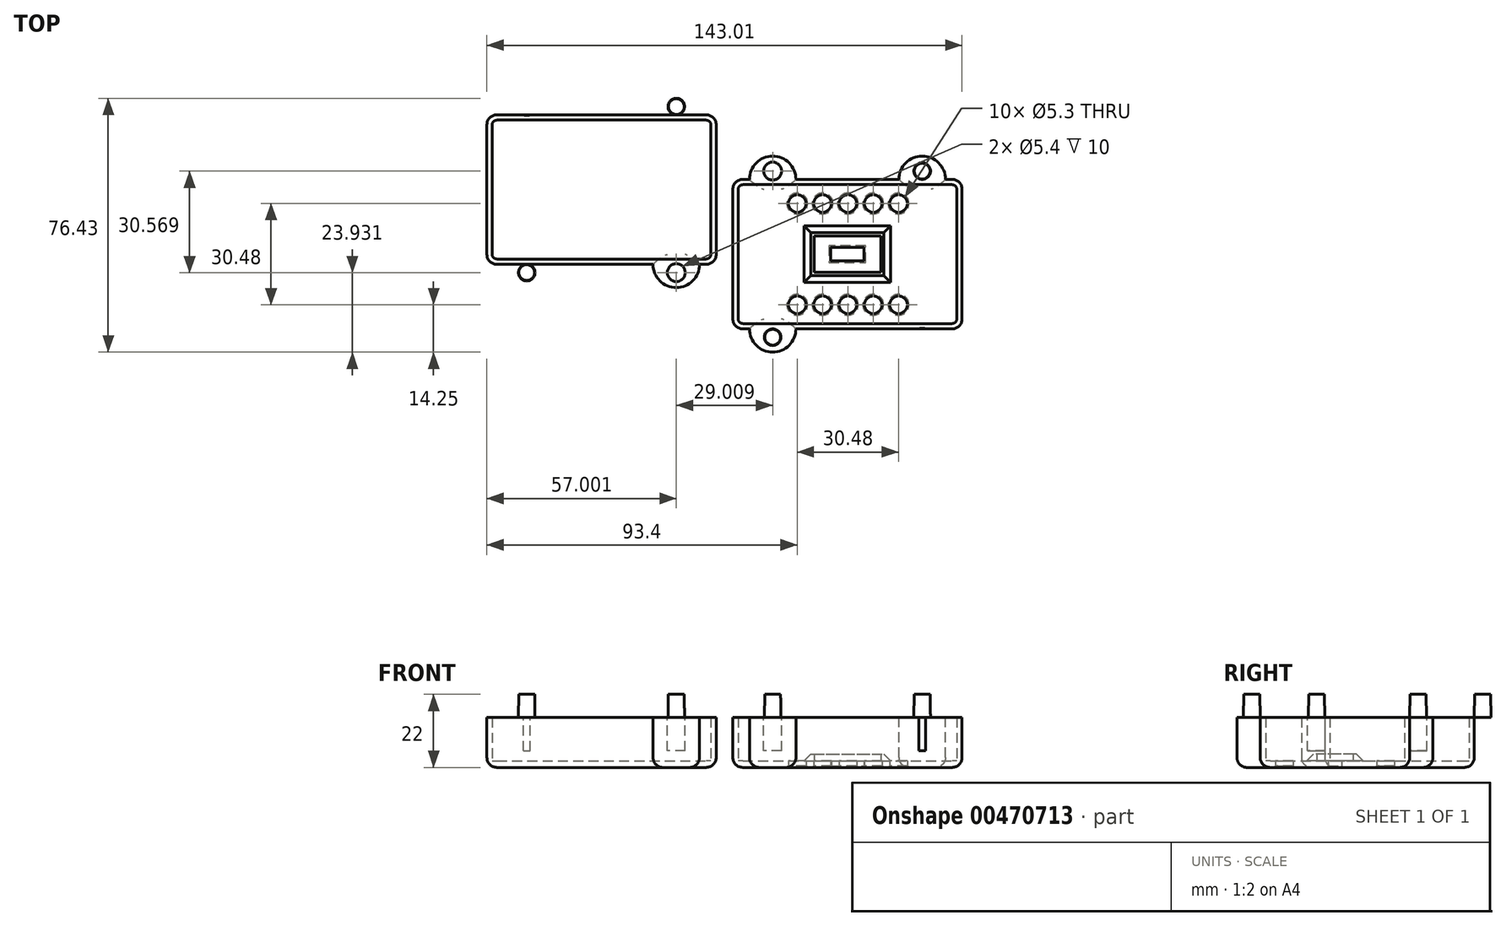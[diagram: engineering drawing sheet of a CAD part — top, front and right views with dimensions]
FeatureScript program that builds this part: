
annotation { "Feature Type Name" : "Feature", "Feature Type Description" : "" }
export const myFeature = defineFeature(function(context is Context, id is Id, definition is map)
    precondition{}
    {
        {
            var Q0;
            Q0=qCreatedBy(makeId("Top.planeOp"),FACE);
            var sketch = newSketch(context, id + "F0", { "sketchPlane" : qUnion([Q0])});
            skLineSegment(sketch, "E0.bottom", {"start": v(3, 0) * mm, "end": v(66, 0) * mm});
            skLineSegment(sketch, "E0.top", {"start": v(3, 45) * mm, "end": v(66, 45) * mm});
            skLineSegment(sketch, "E0.left", {"start": v(0, 3) * mm, "end": v(0, 42) * mm});
            skLineSegment(sketch, "E0.right", {"start": v(69, 3) * mm, "end": v(69, 42) * mm});
            skPoint(sketch, "E1.visualSharp", {"position": v(0, 45) * mm});
            skArc(sketch, "E1.filletArc", {"start": v(3, 45) * mm, "mid": v(0.88, 44.12) * mm, "end": v(0, 42) * mm});
            skPoint(sketch, "E2.visualSharp", {"position": v(69, 45) * mm});
            skArc(sketch, "E2.filletArc", {"start": v(69, 42) * mm, "mid": v(68.12, 44.12) * mm, "end": v(66, 45) * mm});
            skPoint(sketch, "E3.visualSharp", {"position": v(0, 0) * mm});
            skArc(sketch, "E3.filletArc", {"start": v(0, 3) * mm, "mid": v(0.88, 0.88) * mm, "end": v(3, 0) * mm});
            skPoint(sketch, "E4.visualSharp", {"position": v(69, 0) * mm});
            skArc(sketch, "E4.filletArc", {"start": v(66, 0) * mm, "mid": v(68.12, 0.88) * mm, "end": v(69, 3) * mm});
            skLineSegment(sketch, "E5.0", {"start": v(3, 43.4) * mm, "end": v(67.13, 43.4) * mm});
            skLineSegment(sketch, "E6.0", {"start": v(1.6, 3) * mm, "end": v(1.6, 42) * mm});
            skLineSegment(sketch, "E7.0", {"start": v(67.4, 3) * mm, "end": v(67.4, 42) * mm});
            skLineSegment(sketch, "E8.0", {"start": v(3, 1.6) * mm, "end": v(67.13, 1.6) * mm});
            skPoint(sketch, "E9", {"position": v(34.5, 22.5) * mm});
            skPoint(sketch, "E9.positionSnap0", {"position": v(0, 22.5) * mm});
            skPoint(sketch, "E9.positionSnap1", {"position": v(34.5, 45) * mm});
            skLineSegment(sketch, "E10.bottom", {"start": v(4.5, 42.5) * mm, "end": v(64.5, 42.5) * mm});
            skLineSegment(sketch, "E10.top", {"start": v(4.5, 2.5) * mm, "end": v(64.5, 2.5) * mm});
            skLineSegment(sketch, "E10.left", {"start": v(4.5, 42.5) * mm, "end": v(4.5, 2.5) * mm});
            skLineSegment(sketch, "E10.right", {"start": v(64.5, 42.5) * mm, "end": v(64.5, 2.5) * mm});
            skLineSegment(sketch, "E11", {"start": v(34.5, 42.5) * mm, "end": v(34.5, 2.5) * mm, "construction": true});
            skLineSegment(sketch, "E12", {"start": v(4.5, 22.5) * mm, "end": v(64.5, 22.5) * mm, "construction": true});
            skCircle(sketch, "E13", {"center": v(6.5, 40.5) * mm, "radius": 1 * mm});
            skCircle(sketch, "E14", {"center": v(62.5, 40.5) * mm, "radius": 1 * mm});
            skCircle(sketch, "E15", {"center": v(62.5, 4.5) * mm, "radius": 1 * mm});
            skCircle(sketch, "E16", {"center": v(6.5, 4.5) * mm, "radius": 1 * mm});
            skLineSegment(sketch, "E17.0", {"start": v(2.5, 39) * mm, "end": v(62.5, 39) * mm, "construction": true});
            skLineSegment(sketch, "E18.0", {"start": v(2.5, 6) * mm, "end": v(62.5, 6) * mm, "construction": true});
            skLineSegment(sketch, "E19.0", {"start": v(58.5, 42.5) * mm, "end": v(58.5, 2.5) * mm, "construction": true});
            skLineSegment(sketch, "E20.0", {"start": v(10.5, 42.5) * mm, "end": v(10.5, 2.5) * mm, "construction": true});
            skCircle(sketch, "E21", {"center": v(10.5, 39) * mm, "radius": 0.5 * mm, "construction": true});
            skCircle(sketch, "E22.1.0.0", {"center": v(13.04, 39) * mm, "radius": 0.5 * mm, "construction": true});
            skCircle(sketch, "E22.2.0.0", {"center": v(15.58, 39) * mm, "radius": 0.5 * mm, "construction": true});
            skCircle(sketch, "E22.3.0.0", {"center": v(18.12, 39) * mm, "radius": 0.5 * mm, "construction": true});
            skCircle(sketch, "E22.4.0.0", {"center": v(20.66, 39) * mm, "radius": 0.5 * mm, "construction": true});
            skCircle(sketch, "E22.5.0.0", {"center": v(23.2, 39) * mm, "radius": 0.5 * mm, "construction": true});
            skCircle(sketch, "E22.6.0.0", {"center": v(25.74, 39) * mm, "radius": 0.5 * mm, "construction": true});
            skCircle(sketch, "E22.7.0.0", {"center": v(28.28, 39) * mm, "radius": 0.5 * mm, "construction": true});
            skCircle(sketch, "E22.8.0.0", {"center": v(30.82, 39) * mm, "radius": 0.5 * mm, "construction": true});
            skCircle(sketch, "E22.9.0.0", {"center": v(33.36, 39) * mm, "radius": 0.5 * mm, "construction": true});
            skCircle(sketch, "E22.10.0.0", {"center": v(35.9, 39) * mm, "radius": 0.5 * mm, "construction": true});
            skCircle(sketch, "E22.11.0.0", {"center": v(38.44, 39) * mm, "radius": 0.5 * mm, "construction": true});
            skCircle(sketch, "E22.12.0.0", {"center": v(40.98, 39) * mm, "radius": 0.5 * mm, "construction": true});
            skCircle(sketch, "E22.13.0.0", {"center": v(43.52, 39) * mm, "radius": 0.5 * mm, "construction": true});
            skCircle(sketch, "E22.14.0.0", {"center": v(46.06, 39) * mm, "radius": 0.5 * mm, "construction": true});
            skCircle(sketch, "E22.15.0.0", {"center": v(48.6, 39) * mm, "radius": 0.5 * mm, "construction": true});
            skCircle(sketch, "E22.16.0.0", {"center": v(51.14, 39) * mm, "radius": 0.5 * mm, "construction": true});
            skCircle(sketch, "E22.17.0.0", {"center": v(53.68, 39) * mm, "radius": 0.5 * mm, "construction": true});
            skCircle(sketch, "E22.18.0.0", {"center": v(56.22, 39) * mm, "radius": 0.5 * mm, "construction": true});
            skCircle(sketch, "E22.19.0.0", {"center": v(58.76, 39) * mm, "radius": 0.5 * mm, "construction": true});
            skLineSegment(sketch, "E22.direction1", {"start": v(10.5, 39) * mm, "end": v(13.04, 39) * mm, "construction": true});
            skCircle(sketch, "E23.1.0.0", {"center": v(10.5, 36.46) * mm, "radius": 0.5 * mm, "construction": true});
            skCircle(sketch, "E23.1.0.1", {"center": v(11.04, 36.46) * mm, "radius": 0.5 * mm, "construction": true});
            skCircle(sketch, "E23.1.0.2", {"center": v(13.58, 36.46) * mm, "radius": 0.5 * mm, "construction": true});
            skCircle(sketch, "E23.1.0.3", {"center": v(18.12, 36.46) * mm, "radius": 0.5 * mm, "construction": true});
            skCircle(sketch, "E23.1.0.4", {"center": v(18.66, 36.46) * mm, "radius": 0.5 * mm, "construction": true});
            skCircle(sketch, "E23.1.0.5", {"center": v(21.2, 36.46) * mm, "radius": 0.5 * mm, "construction": true});
            skCircle(sketch, "E23.1.0.6", {"center": v(25.74, 36.46) * mm, "radius": 0.5 * mm, "construction": true});
            skCircle(sketch, "E23.1.0.7", {"center": v(26.28, 36.46) * mm, "radius": 0.5 * mm, "construction": true});
            skCircle(sketch, "E23.1.0.8", {"center": v(28.82, 36.46) * mm, "radius": 0.5 * mm, "construction": true});
            skCircle(sketch, "E23.1.0.9", {"center": v(33.36, 36.46) * mm, "radius": 0.5 * mm, "construction": true});
            skCircle(sketch, "E23.1.0.10", {"center": v(33.9, 36.46) * mm, "radius": 0.5 * mm, "construction": true});
            skCircle(sketch, "E23.1.0.11", {"center": v(36.44, 36.46) * mm, "radius": 0.5 * mm, "construction": true});
            skCircle(sketch, "E23.1.0.12", {"center": v(40.98, 36.46) * mm, "radius": 0.5 * mm, "construction": true});
            skCircle(sketch, "E23.1.0.13", {"center": v(41.52, 36.46) * mm, "radius": 0.5 * mm, "construction": true});
            skCircle(sketch, "E23.1.0.14", {"center": v(44.06, 36.46) * mm, "radius": 0.5 * mm, "construction": true});
            skCircle(sketch, "E23.1.0.15", {"center": v(48.6, 36.46) * mm, "radius": 0.5 * mm, "construction": true});
            skCircle(sketch, "E23.1.0.16", {"center": v(49.14, 36.46) * mm, "radius": 0.5 * mm, "construction": true});
            skCircle(sketch, "E23.1.0.17", {"center": v(51.68, 36.46) * mm, "radius": 0.5 * mm, "construction": true});
            skCircle(sketch, "E23.1.0.18", {"center": v(54.22, 36.46) * mm, "radius": 0.5 * mm, "construction": true});
            skCircle(sketch, "E23.1.0.19", {"center": v(56.76, 36.46) * mm, "radius": 0.5 * mm, "construction": true});
            skCircle(sketch, "E23.2.0.0", {"center": v(8.5, 33.92) * mm, "radius": 0.5 * mm, "construction": true});
            skCircle(sketch, "E23.2.0.1", {"center": v(11.04, 33.92) * mm, "radius": 0.5 * mm, "construction": true});
            skCircle(sketch, "E23.2.0.2", {"center": v(13.58, 33.92) * mm, "radius": 0.5 * mm, "construction": true});
            skCircle(sketch, "E23.2.0.3", {"center": v(16.12, 33.92) * mm, "radius": 0.5 * mm, "construction": true});
            skCircle(sketch, "E23.2.0.4", {"center": v(18.66, 33.92) * mm, "radius": 0.5 * mm, "construction": true});
            skCircle(sketch, "E23.2.0.5", {"center": v(21.2, 33.92) * mm, "radius": 0.5 * mm, "construction": true});
            skCircle(sketch, "E23.2.0.6", {"center": v(23.74, 33.92) * mm, "radius": 0.5 * mm, "construction": true});
            skCircle(sketch, "E23.2.0.7", {"center": v(26.28, 33.92) * mm, "radius": 0.5 * mm, "construction": true});
            skCircle(sketch, "E23.2.0.8", {"center": v(28.82, 33.92) * mm, "radius": 0.5 * mm, "construction": true});
            skCircle(sketch, "E23.2.0.9", {"center": v(31.36, 33.92) * mm, "radius": 0.5 * mm, "construction": true});
            skCircle(sketch, "E23.2.0.10", {"center": v(33.9, 33.92) * mm, "radius": 0.5 * mm, "construction": true});
            skCircle(sketch, "E23.2.0.11", {"center": v(36.44, 33.92) * mm, "radius": 0.5 * mm, "construction": true});
            skCircle(sketch, "E23.2.0.12", {"center": v(38.98, 33.92) * mm, "radius": 0.5 * mm, "construction": true});
            skCircle(sketch, "E23.2.0.13", {"center": v(41.52, 33.92) * mm, "radius": 0.5 * mm, "construction": true});
            skCircle(sketch, "E23.2.0.14", {"center": v(44.06, 33.92) * mm, "radius": 0.5 * mm, "construction": true});
            skCircle(sketch, "E23.2.0.15", {"center": v(46.6, 33.92) * mm, "radius": 0.5 * mm, "construction": true});
            skCircle(sketch, "E23.2.0.16", {"center": v(49.14, 33.92) * mm, "radius": 0.5 * mm, "construction": true});
            skCircle(sketch, "E23.2.0.17", {"center": v(51.68, 33.92) * mm, "radius": 0.5 * mm, "construction": true});
            skCircle(sketch, "E23.2.0.18", {"center": v(54.22, 33.92) * mm, "radius": 0.5 * mm, "construction": true});
            skCircle(sketch, "E23.2.0.19", {"center": v(56.76, 33.92) * mm, "radius": 0.5 * mm, "construction": true});
            skCircle(sketch, "E23.3.0.0", {"center": v(8.5, 31.38) * mm, "radius": 0.5 * mm, "construction": true});
            skCircle(sketch, "E23.3.0.1", {"center": v(11.04, 31.38) * mm, "radius": 0.5 * mm, "construction": true});
            skCircle(sketch, "E23.3.0.2", {"center": v(13.58, 31.38) * mm, "radius": 0.5 * mm, "construction": true});
            skCircle(sketch, "E23.3.0.3", {"center": v(16.12, 31.38) * mm, "radius": 0.5 * mm, "construction": true});
            skCircle(sketch, "E23.3.0.4", {"center": v(18.66, 31.38) * mm, "radius": 0.5 * mm, "construction": true});
            skCircle(sketch, "E23.3.0.5", {"center": v(21.2, 31.38) * mm, "radius": 0.5 * mm, "construction": true});
            skCircle(sketch, "E23.3.0.6", {"center": v(23.74, 31.38) * mm, "radius": 0.5 * mm, "construction": true});
            skCircle(sketch, "E23.3.0.7", {"center": v(26.28, 31.38) * mm, "radius": 0.5 * mm, "construction": true});
            skCircle(sketch, "E23.3.0.8", {"center": v(28.82, 31.38) * mm, "radius": 0.5 * mm, "construction": true});
            skCircle(sketch, "E23.3.0.9", {"center": v(31.36, 31.38) * mm, "radius": 0.5 * mm, "construction": true});
            skCircle(sketch, "E23.3.0.10", {"center": v(33.9, 31.38) * mm, "radius": 0.5 * mm, "construction": true});
            skCircle(sketch, "E23.3.0.11", {"center": v(36.44, 31.38) * mm, "radius": 0.5 * mm, "construction": true});
            skCircle(sketch, "E23.3.0.12", {"center": v(38.98, 31.38) * mm, "radius": 0.5 * mm, "construction": true});
            skCircle(sketch, "E23.3.0.13", {"center": v(41.52, 31.38) * mm, "radius": 0.5 * mm, "construction": true});
            skCircle(sketch, "E23.3.0.14", {"center": v(44.06, 31.38) * mm, "radius": 0.5 * mm, "construction": true});
            skCircle(sketch, "E23.3.0.15", {"center": v(46.6, 31.38) * mm, "radius": 0.5 * mm, "construction": true});
            skCircle(sketch, "E23.3.0.16", {"center": v(49.14, 31.38) * mm, "radius": 0.5 * mm, "construction": true});
            skCircle(sketch, "E23.3.0.17", {"center": v(51.68, 31.38) * mm, "radius": 0.5 * mm, "construction": true});
            skCircle(sketch, "E23.3.0.18", {"center": v(54.22, 31.38) * mm, "radius": 0.5 * mm, "construction": true});
            skCircle(sketch, "E23.3.0.19", {"center": v(56.76, 31.38) * mm, "radius": 0.5 * mm, "construction": true});
            skCircle(sketch, "E23.4.0.0", {"center": v(8.5, 28.84) * mm, "radius": 0.5 * mm, "construction": true});
            skCircle(sketch, "E23.4.0.1", {"center": v(11.04, 28.84) * mm, "radius": 0.5 * mm, "construction": true});
            skCircle(sketch, "E23.4.0.2", {"center": v(13.58, 28.84) * mm, "radius": 0.5 * mm, "construction": true});
            skCircle(sketch, "E23.4.0.3", {"center": v(16.12, 28.84) * mm, "radius": 0.5 * mm, "construction": true});
            skCircle(sketch, "E23.4.0.4", {"center": v(18.66, 28.84) * mm, "radius": 0.5 * mm, "construction": true});
            skCircle(sketch, "E23.4.0.5", {"center": v(21.2, 28.84) * mm, "radius": 0.5 * mm, "construction": true});
            skCircle(sketch, "E23.4.0.6", {"center": v(23.74, 28.84) * mm, "radius": 0.5 * mm, "construction": true});
            skCircle(sketch, "E23.4.0.7", {"center": v(26.28, 28.84) * mm, "radius": 0.5 * mm, "construction": true});
            skCircle(sketch, "E23.4.0.8", {"center": v(28.82, 28.84) * mm, "radius": 0.5 * mm, "construction": true});
            skCircle(sketch, "E23.4.0.9", {"center": v(31.36, 28.84) * mm, "radius": 0.5 * mm, "construction": true});
            skCircle(sketch, "E23.4.0.10", {"center": v(33.9, 28.84) * mm, "radius": 0.5 * mm, "construction": true});
            skCircle(sketch, "E23.4.0.11", {"center": v(36.44, 28.84) * mm, "radius": 0.5 * mm, "construction": true});
            skCircle(sketch, "E23.4.0.12", {"center": v(38.98, 28.84) * mm, "radius": 0.5 * mm, "construction": true});
            skCircle(sketch, "E23.4.0.13", {"center": v(41.52, 28.84) * mm, "radius": 0.5 * mm, "construction": true});
            skCircle(sketch, "E23.4.0.14", {"center": v(44.06, 28.84) * mm, "radius": 0.5 * mm, "construction": true});
            skCircle(sketch, "E23.4.0.15", {"center": v(46.6, 28.84) * mm, "radius": 0.5 * mm, "construction": true});
            skCircle(sketch, "E23.4.0.16", {"center": v(49.14, 28.84) * mm, "radius": 0.5 * mm, "construction": true});
            skCircle(sketch, "E23.4.0.17", {"center": v(51.68, 28.84) * mm, "radius": 0.5 * mm, "construction": true});
            skCircle(sketch, "E23.4.0.18", {"center": v(54.22, 28.84) * mm, "radius": 0.5 * mm, "construction": true});
            skCircle(sketch, "E23.4.0.19", {"center": v(56.76, 28.84) * mm, "radius": 0.5 * mm, "construction": true});
            skCircle(sketch, "E23.5.0.0", {"center": v(8.5, 26.3) * mm, "radius": 0.5 * mm, "construction": true});
            skCircle(sketch, "E23.5.0.1", {"center": v(11.04, 26.3) * mm, "radius": 0.5 * mm, "construction": true});
            skCircle(sketch, "E23.5.0.2", {"center": v(13.58, 26.3) * mm, "radius": 0.5 * mm, "construction": true});
            skCircle(sketch, "E23.5.0.3", {"center": v(16.12, 26.3) * mm, "radius": 0.5 * mm, "construction": true});
            skCircle(sketch, "E23.5.0.4", {"center": v(18.66, 26.3) * mm, "radius": 0.5 * mm, "construction": true});
            skCircle(sketch, "E23.5.0.5", {"center": v(21.2, 26.3) * mm, "radius": 0.5 * mm, "construction": true});
            skCircle(sketch, "E23.5.0.6", {"center": v(23.74, 26.3) * mm, "radius": 0.5 * mm, "construction": true});
            skCircle(sketch, "E23.5.0.7", {"center": v(26.28, 26.3) * mm, "radius": 0.5 * mm, "construction": true});
            skCircle(sketch, "E23.5.0.8", {"center": v(28.82, 26.3) * mm, "radius": 0.5 * mm, "construction": true});
            skCircle(sketch, "E23.5.0.9", {"center": v(31.36, 26.3) * mm, "radius": 0.5 * mm, "construction": true});
            skCircle(sketch, "E23.5.0.10", {"center": v(33.9, 26.3) * mm, "radius": 0.5 * mm, "construction": true});
            skCircle(sketch, "E23.5.0.11", {"center": v(36.44, 26.3) * mm, "radius": 0.5 * mm, "construction": true});
            skCircle(sketch, "E23.5.0.12", {"center": v(38.98, 26.3) * mm, "radius": 0.5 * mm, "construction": true});
            skCircle(sketch, "E23.5.0.13", {"center": v(41.52, 26.3) * mm, "radius": 0.5 * mm, "construction": true});
            skCircle(sketch, "E23.5.0.14", {"center": v(44.06, 26.3) * mm, "radius": 0.5 * mm, "construction": true});
            skCircle(sketch, "E23.5.0.15", {"center": v(46.6, 26.3) * mm, "radius": 0.5 * mm, "construction": true});
            skCircle(sketch, "E23.5.0.16", {"center": v(49.14, 26.3) * mm, "radius": 0.5 * mm, "construction": true});
            skCircle(sketch, "E23.5.0.17", {"center": v(51.68, 26.3) * mm, "radius": 0.5 * mm, "construction": true});
            skCircle(sketch, "E23.5.0.18", {"center": v(54.22, 26.3) * mm, "radius": 0.5 * mm, "construction": true});
            skCircle(sketch, "E23.5.0.19", {"center": v(56.76, 26.3) * mm, "radius": 0.5 * mm, "construction": true});
            skCircle(sketch, "E23.6.0.0", {"center": v(8.5, 23.76) * mm, "radius": 0.5 * mm, "construction": true});
            skCircle(sketch, "E23.6.0.1", {"center": v(11.04, 23.76) * mm, "radius": 0.5 * mm, "construction": true});
            skCircle(sketch, "E23.6.0.2", {"center": v(13.58, 23.76) * mm, "radius": 0.5 * mm, "construction": true});
            skCircle(sketch, "E23.6.0.3", {"center": v(16.12, 23.76) * mm, "radius": 0.5 * mm, "construction": true});
            skCircle(sketch, "E23.6.0.4", {"center": v(18.66, 23.76) * mm, "radius": 0.5 * mm, "construction": true});
            skCircle(sketch, "E23.6.0.5", {"center": v(21.2, 23.76) * mm, "radius": 0.5 * mm, "construction": true});
            skCircle(sketch, "E23.6.0.6", {"center": v(23.74, 23.76) * mm, "radius": 0.5 * mm, "construction": true});
            skCircle(sketch, "E23.6.0.7", {"center": v(26.28, 23.76) * mm, "radius": 0.5 * mm, "construction": true});
            skCircle(sketch, "E23.6.0.8", {"center": v(28.82, 23.76) * mm, "radius": 0.5 * mm, "construction": true});
            skCircle(sketch, "E23.6.0.9", {"center": v(31.36, 23.76) * mm, "radius": 0.5 * mm, "construction": true});
            skCircle(sketch, "E23.6.0.10", {"center": v(33.9, 23.76) * mm, "radius": 0.5 * mm, "construction": true});
            skCircle(sketch, "E23.6.0.11", {"center": v(36.44, 23.76) * mm, "radius": 0.5 * mm, "construction": true});
            skCircle(sketch, "E23.6.0.12", {"center": v(38.98, 23.76) * mm, "radius": 0.5 * mm, "construction": true});
            skCircle(sketch, "E23.6.0.13", {"center": v(41.52, 23.76) * mm, "radius": 0.5 * mm, "construction": true});
            skCircle(sketch, "E23.6.0.14", {"center": v(44.06, 23.76) * mm, "radius": 0.5 * mm, "construction": true});
            skCircle(sketch, "E23.6.0.15", {"center": v(46.6, 23.76) * mm, "radius": 0.5 * mm, "construction": true});
            skCircle(sketch, "E23.6.0.16", {"center": v(49.14, 23.76) * mm, "radius": 0.5 * mm, "construction": true});
            skCircle(sketch, "E23.6.0.17", {"center": v(51.68, 23.76) * mm, "radius": 0.5 * mm, "construction": true});
            skCircle(sketch, "E23.6.0.18", {"center": v(54.22, 23.76) * mm, "radius": 0.5 * mm, "construction": true});
            skCircle(sketch, "E23.6.0.19", {"center": v(56.76, 23.76) * mm, "radius": 0.5 * mm, "construction": true});
            skCircle(sketch, "E23.7.0.0", {"center": v(8.5, 21.22) * mm, "radius": 0.5 * mm, "construction": true});
            skCircle(sketch, "E23.7.0.1", {"center": v(11.04, 21.22) * mm, "radius": 0.5 * mm, "construction": true});
            skCircle(sketch, "E23.7.0.2", {"center": v(13.58, 21.22) * mm, "radius": 0.5 * mm, "construction": true});
            skCircle(sketch, "E23.7.0.3", {"center": v(16.12, 21.22) * mm, "radius": 0.5 * mm, "construction": true});
            skCircle(sketch, "E23.7.0.4", {"center": v(18.66, 21.22) * mm, "radius": 0.5 * mm, "construction": true});
            skCircle(sketch, "E23.7.0.5", {"center": v(21.2, 21.22) * mm, "radius": 0.5 * mm, "construction": true});
            skCircle(sketch, "E23.7.0.6", {"center": v(23.74, 21.22) * mm, "radius": 0.5 * mm, "construction": true});
            skCircle(sketch, "E23.7.0.7", {"center": v(26.28, 21.22) * mm, "radius": 0.5 * mm, "construction": true});
            skCircle(sketch, "E23.7.0.8", {"center": v(28.82, 21.22) * mm, "radius": 0.5 * mm, "construction": true});
            skCircle(sketch, "E23.7.0.9", {"center": v(31.36, 21.22) * mm, "radius": 0.5 * mm, "construction": true});
            skCircle(sketch, "E23.7.0.10", {"center": v(33.9, 21.22) * mm, "radius": 0.5 * mm, "construction": true});
            skCircle(sketch, "E23.7.0.11", {"center": v(36.44, 21.22) * mm, "radius": 0.5 * mm, "construction": true});
            skCircle(sketch, "E23.7.0.12", {"center": v(38.98, 21.22) * mm, "radius": 0.5 * mm, "construction": true});
            skCircle(sketch, "E23.7.0.13", {"center": v(41.52, 21.22) * mm, "radius": 0.5 * mm, "construction": true});
            skCircle(sketch, "E23.7.0.14", {"center": v(44.06, 21.22) * mm, "radius": 0.5 * mm, "construction": true});
            skCircle(sketch, "E23.7.0.15", {"center": v(46.6, 21.22) * mm, "radius": 0.5 * mm, "construction": true});
            skCircle(sketch, "E23.7.0.16", {"center": v(49.14, 21.22) * mm, "radius": 0.5 * mm, "construction": true});
            skCircle(sketch, "E23.7.0.17", {"center": v(51.68, 21.22) * mm, "radius": 0.5 * mm, "construction": true});
            skCircle(sketch, "E23.7.0.18", {"center": v(54.22, 21.22) * mm, "radius": 0.5 * mm, "construction": true});
            skCircle(sketch, "E23.7.0.19", {"center": v(56.76, 21.22) * mm, "radius": 0.5 * mm, "construction": true});
            skCircle(sketch, "E23.8.0.0", {"center": v(8.5, 18.68) * mm, "radius": 0.5 * mm, "construction": true});
            skCircle(sketch, "E23.8.0.1", {"center": v(11.04, 18.68) * mm, "radius": 0.5 * mm, "construction": true});
            skCircle(sketch, "E23.8.0.2", {"center": v(13.58, 18.68) * mm, "radius": 0.5 * mm, "construction": true});
            skCircle(sketch, "E23.8.0.3", {"center": v(16.12, 18.68) * mm, "radius": 0.5 * mm, "construction": true});
            skCircle(sketch, "E23.8.0.4", {"center": v(18.66, 18.68) * mm, "radius": 0.5 * mm, "construction": true});
            skCircle(sketch, "E23.8.0.5", {"center": v(21.2, 18.68) * mm, "radius": 0.5 * mm, "construction": true});
            skCircle(sketch, "E23.8.0.6", {"center": v(23.74, 18.68) * mm, "radius": 0.5 * mm, "construction": true});
            skCircle(sketch, "E23.8.0.7", {"center": v(26.28, 18.68) * mm, "radius": 0.5 * mm, "construction": true});
            skCircle(sketch, "E23.8.0.8", {"center": v(28.82, 18.68) * mm, "radius": 0.5 * mm, "construction": true});
            skCircle(sketch, "E23.8.0.9", {"center": v(31.36, 18.68) * mm, "radius": 0.5 * mm, "construction": true});
            skCircle(sketch, "E23.8.0.10", {"center": v(33.9, 18.68) * mm, "radius": 0.5 * mm, "construction": true});
            skCircle(sketch, "E23.8.0.11", {"center": v(36.44, 18.68) * mm, "radius": 0.5 * mm, "construction": true});
            skCircle(sketch, "E23.8.0.12", {"center": v(38.98, 18.68) * mm, "radius": 0.5 * mm, "construction": true});
            skCircle(sketch, "E23.8.0.13", {"center": v(41.52, 18.68) * mm, "radius": 0.5 * mm, "construction": true});
            skCircle(sketch, "E23.8.0.14", {"center": v(44.06, 18.68) * mm, "radius": 0.5 * mm, "construction": true});
            skCircle(sketch, "E23.8.0.15", {"center": v(46.6, 18.68) * mm, "radius": 0.5 * mm, "construction": true});
            skCircle(sketch, "E23.8.0.16", {"center": v(49.14, 18.68) * mm, "radius": 0.5 * mm, "construction": true});
            skCircle(sketch, "E23.8.0.17", {"center": v(51.68, 18.68) * mm, "radius": 0.5 * mm, "construction": true});
            skCircle(sketch, "E23.8.0.18", {"center": v(54.22, 18.68) * mm, "radius": 0.5 * mm, "construction": true});
            skCircle(sketch, "E23.8.0.19", {"center": v(56.76, 18.68) * mm, "radius": 0.5 * mm, "construction": true});
            skCircle(sketch, "E23.9.0.0", {"center": v(8.5, 16.14) * mm, "radius": 0.5 * mm, "construction": true});
            skCircle(sketch, "E23.9.0.1", {"center": v(11.04, 16.14) * mm, "radius": 0.5 * mm, "construction": true});
            skCircle(sketch, "E23.9.0.2", {"center": v(13.58, 16.14) * mm, "radius": 0.5 * mm, "construction": true});
            skCircle(sketch, "E23.9.0.3", {"center": v(16.12, 16.14) * mm, "radius": 0.5 * mm, "construction": true});
            skCircle(sketch, "E23.9.0.4", {"center": v(18.66, 16.14) * mm, "radius": 0.5 * mm, "construction": true});
            skCircle(sketch, "E23.9.0.5", {"center": v(21.2, 16.14) * mm, "radius": 0.5 * mm, "construction": true});
            skCircle(sketch, "E23.9.0.6", {"center": v(23.74, 16.14) * mm, "radius": 0.5 * mm, "construction": true});
            skCircle(sketch, "E23.9.0.7", {"center": v(26.28, 16.14) * mm, "radius": 0.5 * mm, "construction": true});
            skCircle(sketch, "E23.9.0.8", {"center": v(30.1, 16.14) * mm, "radius": 0.5 * mm, "construction": true});
            skCircle(sketch, "E23.9.0.9", {"center": v(31.36, 16.14) * mm, "radius": 0.5 * mm, "construction": true});
            skCircle(sketch, "E23.9.0.10", {"center": v(33.9, 16.14) * mm, "radius": 0.5 * mm, "construction": true});
            skCircle(sketch, "E23.9.0.11", {"center": v(36.44, 16.14) * mm, "radius": 0.5 * mm, "construction": true});
            skCircle(sketch, "E23.9.0.12", {"center": v(38.98, 16.14) * mm, "radius": 0.5 * mm, "construction": true});
            skCircle(sketch, "E23.9.0.13", {"center": v(41.52, 16.14) * mm, "radius": 0.5 * mm, "construction": true});
            skCircle(sketch, "E23.9.0.14", {"center": v(44.06, 16.14) * mm, "radius": 0.5 * mm, "construction": true});
            skCircle(sketch, "E23.9.0.15", {"center": v(46.6, 16.14) * mm, "radius": 0.5 * mm, "construction": true});
            skCircle(sketch, "E23.9.0.16", {"center": v(49.14, 16.14) * mm, "radius": 0.5 * mm, "construction": true});
            skCircle(sketch, "E23.9.0.17", {"center": v(51.68, 16.14) * mm, "radius": 0.5 * mm, "construction": true});
            skCircle(sketch, "E23.9.0.18", {"center": v(54.22, 16.14) * mm, "radius": 0.5 * mm, "construction": true});
            skCircle(sketch, "E23.9.0.19", {"center": v(56.76, 16.14) * mm, "radius": 0.5 * mm, "construction": true});
            skCircle(sketch, "E23.10.0.0", {"center": v(8.5, 13.6) * mm, "radius": 0.5 * mm, "construction": true});
            skCircle(sketch, "E23.10.0.1", {"center": v(11.04, 13.6) * mm, "radius": 0.5 * mm, "construction": true});
            skCircle(sketch, "E23.10.0.2", {"center": v(13.58, 13.6) * mm, "radius": 0.5 * mm, "construction": true});
            skCircle(sketch, "E23.10.0.3", {"center": v(16.12, 13.6) * mm, "radius": 0.5 * mm, "construction": true});
            skCircle(sketch, "E23.10.0.4", {"center": v(18.66, 13.6) * mm, "radius": 0.5 * mm, "construction": true});
            skCircle(sketch, "E23.10.0.5", {"center": v(21.2, 13.6) * mm, "radius": 0.5 * mm, "construction": true});
            skCircle(sketch, "E23.10.0.6", {"center": v(23.74, 13.6) * mm, "radius": 0.5 * mm, "construction": true});
            skCircle(sketch, "E23.10.0.7", {"center": v(26.28, 13.6) * mm, "radius": 0.5 * mm, "construction": true});
            skCircle(sketch, "E23.10.0.8", {"center": v(28.82, 13.6) * mm, "radius": 0.5 * mm, "construction": true});
            skCircle(sketch, "E23.10.0.9", {"center": v(31.36, 13.6) * mm, "radius": 0.5 * mm, "construction": true});
            skCircle(sketch, "E23.10.0.10", {"center": v(33.9, 13.6) * mm, "radius": 0.5 * mm, "construction": true});
            skCircle(sketch, "E23.10.0.11", {"center": v(36.44, 13.6) * mm, "radius": 0.5 * mm, "construction": true});
            skCircle(sketch, "E23.10.0.12", {"center": v(38.98, 13.6) * mm, "radius": 0.5 * mm, "construction": true});
            skCircle(sketch, "E23.10.0.13", {"center": v(41.52, 13.6) * mm, "radius": 0.5 * mm, "construction": true});
            skCircle(sketch, "E23.10.0.14", {"center": v(44.06, 13.6) * mm, "radius": 0.5 * mm, "construction": true});
            skCircle(sketch, "E23.10.0.15", {"center": v(46.6, 13.6) * mm, "radius": 0.5 * mm, "construction": true});
            skCircle(sketch, "E23.10.0.16", {"center": v(49.14, 13.6) * mm, "radius": 0.5 * mm, "construction": true});
            skCircle(sketch, "E23.10.0.17", {"center": v(51.68, 13.6) * mm, "radius": 0.5 * mm, "construction": true});
            skCircle(sketch, "E23.10.0.18", {"center": v(54.22, 13.6) * mm, "radius": 0.5 * mm, "construction": true});
            skCircle(sketch, "E23.10.0.19", {"center": v(56.76, 13.6) * mm, "radius": 0.5 * mm, "construction": true});
            skCircle(sketch, "E23.11.0.0", {"center": v(8.5, 11.06) * mm, "radius": 0.5 * mm, "construction": true});
            skCircle(sketch, "E23.11.0.1", {"center": v(11.04, 11.06) * mm, "radius": 0.5 * mm, "construction": true});
            skCircle(sketch, "E23.11.0.2", {"center": v(13.58, 11.06) * mm, "radius": 0.5 * mm, "construction": true});
            skCircle(sketch, "E23.11.0.3", {"center": v(16.12, 11.06) * mm, "radius": 0.5 * mm, "construction": true});
            skCircle(sketch, "E23.11.0.4", {"center": v(18.66, 11.06) * mm, "radius": 0.5 * mm, "construction": true});
            skCircle(sketch, "E23.11.0.5", {"center": v(21.2, 11.06) * mm, "radius": 0.5 * mm, "construction": true});
            skCircle(sketch, "E23.11.0.6", {"center": v(23.74, 11.06) * mm, "radius": 0.5 * mm, "construction": true});
            skCircle(sketch, "E23.11.0.7", {"center": v(26.28, 11.06) * mm, "radius": 0.5 * mm, "construction": true});
            skCircle(sketch, "E23.11.0.8", {"center": v(28.82, 11.06) * mm, "radius": 0.5 * mm, "construction": true});
            skCircle(sketch, "E23.11.0.9", {"center": v(31.36, 11.06) * mm, "radius": 0.5 * mm, "construction": true});
            skCircle(sketch, "E23.11.0.10", {"center": v(33.9, 11.06) * mm, "radius": 0.5 * mm, "construction": true});
            skCircle(sketch, "E23.11.0.11", {"center": v(36.44, 11.06) * mm, "radius": 0.5 * mm, "construction": true});
            skCircle(sketch, "E23.11.0.12", {"center": v(38.98, 11.06) * mm, "radius": 0.5 * mm, "construction": true});
            skCircle(sketch, "E23.11.0.13", {"center": v(41.52, 11.06) * mm, "radius": 0.5 * mm, "construction": true});
            skCircle(sketch, "E23.11.0.14", {"center": v(44.06, 11.06) * mm, "radius": 0.5 * mm, "construction": true});
            skCircle(sketch, "E23.11.0.15", {"center": v(46.6, 11.06) * mm, "radius": 0.5 * mm, "construction": true});
            skCircle(sketch, "E23.11.0.16", {"center": v(49.14, 11.06) * mm, "radius": 0.5 * mm, "construction": true});
            skCircle(sketch, "E23.11.0.17", {"center": v(51.68, 11.06) * mm, "radius": 0.5 * mm, "construction": true});
            skCircle(sketch, "E23.11.0.18", {"center": v(54.22, 11.06) * mm, "radius": 0.5 * mm, "construction": true});
            skCircle(sketch, "E23.11.0.19", {"center": v(56.76, 11.06) * mm, "radius": 0.5 * mm, "construction": true});
            skCircle(sketch, "E23.12.0.0", {"center": v(8.5, 8.52) * mm, "radius": 0.5 * mm, "construction": true});
            skCircle(sketch, "E23.12.0.1", {"center": v(11.04, 8.52) * mm, "radius": 0.5 * mm, "construction": true});
            skCircle(sketch, "E23.12.0.2", {"center": v(13.58, 8.52) * mm, "radius": 0.5 * mm, "construction": true});
            skCircle(sketch, "E23.12.0.3", {"center": v(16.12, 8.52) * mm, "radius": 0.5 * mm, "construction": true});
            skCircle(sketch, "E23.12.0.4", {"center": v(18.66, 8.52) * mm, "radius": 0.5 * mm, "construction": true});
            skCircle(sketch, "E23.12.0.5", {"center": v(21.2, 8.52) * mm, "radius": 0.5 * mm, "construction": true});
            skCircle(sketch, "E23.12.0.6", {"center": v(23.74, 8.52) * mm, "radius": 0.5 * mm, "construction": true});
            skCircle(sketch, "E23.12.0.7", {"center": v(26.28, 8.52) * mm, "radius": 0.5 * mm, "construction": true});
            skCircle(sketch, "E23.12.0.8", {"center": v(28.82, 8.52) * mm, "radius": 0.5 * mm, "construction": true});
            skCircle(sketch, "E23.12.0.9", {"center": v(31.36, 8.52) * mm, "radius": 0.5 * mm, "construction": true});
            skCircle(sketch, "E23.12.0.10", {"center": v(33.9, 8.52) * mm, "radius": 0.5 * mm, "construction": true});
            skCircle(sketch, "E23.12.0.11", {"center": v(36.44, 8.52) * mm, "radius": 0.5 * mm, "construction": true});
            skCircle(sketch, "E23.12.0.12", {"center": v(38.98, 8.52) * mm, "radius": 0.5 * mm, "construction": true});
            skCircle(sketch, "E23.12.0.13", {"center": v(41.52, 8.52) * mm, "radius": 0.5 * mm, "construction": true});
            skCircle(sketch, "E23.12.0.14", {"center": v(44.06, 8.52) * mm, "radius": 0.5 * mm, "construction": true});
            skCircle(sketch, "E23.12.0.15", {"center": v(46.6, 8.52) * mm, "radius": 0.5 * mm, "construction": true});
            skCircle(sketch, "E23.12.0.16", {"center": v(49.14, 8.52) * mm, "radius": 0.5 * mm, "construction": true});
            skCircle(sketch, "E23.12.0.17", {"center": v(51.68, 8.52) * mm, "radius": 0.5 * mm, "construction": true});
            skCircle(sketch, "E23.12.0.18", {"center": v(54.22, 8.52) * mm, "radius": 0.5 * mm, "construction": true});
            skCircle(sketch, "E23.12.0.19", {"center": v(56.76, 8.52) * mm, "radius": 0.5 * mm, "construction": true});
            skCircle(sketch, "E23.13.0.0", {"center": v(8.5, 5.98) * mm, "radius": 0.5 * mm, "construction": true});
            skCircle(sketch, "E23.13.0.1", {"center": v(11.04, 5.98) * mm, "radius": 0.5 * mm, "construction": true});
            skCircle(sketch, "E23.13.0.2", {"center": v(13.58, 5.98) * mm, "radius": 0.5 * mm, "construction": true});
            skCircle(sketch, "E23.13.0.3", {"center": v(16.12, 5.98) * mm, "radius": 0.5 * mm, "construction": true});
            skCircle(sketch, "E23.13.0.4", {"center": v(18.66, 5.98) * mm, "radius": 0.5 * mm, "construction": true});
            skCircle(sketch, "E23.13.0.5", {"center": v(21.2, 5.98) * mm, "radius": 0.5 * mm, "construction": true});
            skCircle(sketch, "E23.13.0.6", {"center": v(23.74, 5.98) * mm, "radius": 0.5 * mm, "construction": true});
            skCircle(sketch, "E23.13.0.7", {"center": v(26.28, 5.98) * mm, "radius": 0.5 * mm, "construction": true});
            skCircle(sketch, "E23.13.0.8", {"center": v(28.82, 5.98) * mm, "radius": 0.5 * mm, "construction": true});
            skCircle(sketch, "E23.13.0.9", {"center": v(31.36, 5.98) * mm, "radius": 0.5 * mm, "construction": true});
            skCircle(sketch, "E23.13.0.10", {"center": v(33.9, 5.98) * mm, "radius": 0.5 * mm, "construction": true});
            skCircle(sketch, "E23.13.0.11", {"center": v(36.44, 5.98) * mm, "radius": 0.5 * mm, "construction": true});
            skCircle(sketch, "E23.13.0.12", {"center": v(38.98, 5.98) * mm, "radius": 0.5 * mm, "construction": true});
            skCircle(sketch, "E23.13.0.13", {"center": v(41.52, 5.98) * mm, "radius": 0.5 * mm, "construction": true});
            skCircle(sketch, "E23.13.0.14", {"center": v(44.06, 5.98) * mm, "radius": 0.5 * mm, "construction": true});
            skCircle(sketch, "E23.13.0.15", {"center": v(46.6, 5.98) * mm, "radius": 0.5 * mm, "construction": true});
            skCircle(sketch, "E23.13.0.16", {"center": v(49.14, 5.98) * mm, "radius": 0.5 * mm, "construction": true});
            skCircle(sketch, "E23.13.0.17", {"center": v(51.68, 5.98) * mm, "radius": 0.5 * mm, "construction": true});
            skCircle(sketch, "E23.13.0.18", {"center": v(54.22, 5.98) * mm, "radius": 0.5 * mm, "construction": true});
            skCircle(sketch, "E23.13.0.19", {"center": v(56.76, 5.98) * mm, "radius": 0.5 * mm, "construction": true});
            skLineSegment(sketch, "E23.direction1", {"start": v(10.5, 39) * mm, "end": v(10.5, 36.46) * mm, "construction": true});
            skLineSegment(sketch, "E24", {"start": v(10.5, 39) * mm, "end": v(10.5, 36.46) * mm});
            skLineSegment(sketch, "E25", {"start": v(18.12, 39) * mm, "end": v(18.12, 36.46) * mm});
            skLineSegment(sketch, "E26", {"start": v(25.74, 39) * mm, "end": v(25.74, 36.46) * mm});
            skLineSegment(sketch, "E27", {"start": v(33.36, 39) * mm, "end": v(33.36, 36.46) * mm});
            skLineSegment(sketch, "E28", {"start": v(40.98, 39) * mm, "end": v(40.98, 36.46) * mm});
            skLineSegment(sketch, "E29", {"start": v(48.6, 39) * mm, "end": v(48.6, 36.46) * mm});
            skPoint(sketch, "E30", {"position": v(48.6, 37.73) * mm});
            skPoint(sketch, "E31", {"position": v(40.98, 37.73) * mm});
            skPoint(sketch, "E32", {"position": v(33.36, 37.73) * mm});
            skPoint(sketch, "E33", {"position": v(25.74, 37.73) * mm});
            skPoint(sketch, "E34", {"position": v(18.12, 37.73) * mm});
            skLineSegment(sketch, "E35", {"start": v(16.12, 5.98) * mm, "end": v(16.12, 8.52) * mm});
            skLineSegment(sketch, "E36", {"start": v(23.74, 5.98) * mm, "end": v(23.74, 8.52) * mm});
            skLineSegment(sketch, "E37", {"start": v(31.36, 8.52) * mm, "end": v(31.36, 5.98) * mm});
            skLineSegment(sketch, "E38", {"start": v(38.98, 5.98) * mm, "end": v(38.98, 8.52) * mm});
            skLineSegment(sketch, "E39", {"start": v(46.6, 8.52) * mm, "end": v(46.6, 5.98) * mm});
            skPoint(sketch, "E40", {"position": v(16.12, 7.25) * mm});
            skPoint(sketch, "E41", {"position": v(23.74, 7.25) * mm});
            skPoint(sketch, "E42", {"position": v(31.36, 7.25) * mm});
            skPoint(sketch, "E43", {"position": v(38.98, 7.25) * mm});
            skPoint(sketch, "E44", {"position": v(46.6, 7.25) * mm});
            skCircle(sketch, "E45", {"center": v(19.39, 37.73) * mm, "radius": 2.65 * mm});
            skCircle(sketch, "E46", {"center": v(27, 37.73) * mm, "radius": 2.65 * mm});
            skCircle(sketch, "E47", {"center": v(34.63, 37.73) * mm, "radius": 2.65 * mm});
            skCircle(sketch, "E48", {"center": v(42.25, 37.73) * mm, "radius": 2.65 * mm});
            skCircle(sketch, "E49", {"center": v(49.87, 37.73) * mm, "radius": 2.65 * mm});
            skCircle(sketch, "E50", {"center": v(19.4, 7.25) * mm, "radius": 2.65 * mm});
            skCircle(sketch, "E51", {"center": v(27.01, 7.25) * mm, "radius": 2.65 * mm});
            skCircle(sketch, "E52", {"center": v(34.63, 7.25) * mm, "radius": 2.65 * mm});
            skCircle(sketch, "E53", {"center": v(42.25, 7.25) * mm, "radius": 2.65 * mm});
            skCircle(sketch, "E54", {"center": v(49.87, 7.25) * mm, "radius": 2.65 * mm});
            skLineSegment(sketch, "E55.bottom", {"start": v(24.5, 28) * mm, "end": v(44.5, 28) * mm});
            skLineSegment(sketch, "E55.top", {"start": v(24.5, 17) * mm, "end": v(44.5, 17) * mm});
            skLineSegment(sketch, "E55.left", {"start": v(24.5, 28) * mm, "end": v(24.5, 17) * mm});
            skLineSegment(sketch, "E55.right", {"start": v(44.5, 28) * mm, "end": v(44.5, 17) * mm});
            skLineSegment(sketch, "E56", {"start": v(34.5, 28) * mm, "end": v(34.5, 17) * mm, "construction": true});
            skLineSegment(sketch, "E57", {"start": v(24.5, 22.5) * mm, "end": v(44.5, 22.5) * mm, "construction": true});
            skLineSegment(sketch, "E58.bottom", {"start": v(29.5, 24.5) * mm, "end": v(39.5, 24.5) * mm});
            skLineSegment(sketch, "E58.top", {"start": v(29.5, 20.5) * mm, "end": v(39.5, 20.5) * mm});
            skLineSegment(sketch, "E58.left", {"start": v(29.5, 24.5) * mm, "end": v(29.5, 20.5) * mm});
            skLineSegment(sketch, "E58.right", {"start": v(39.5, 24.5) * mm, "end": v(39.5, 20.5) * mm});
            skLineSegment(sketch, "E59.0", {"start": v(21.5, 31) * mm, "end": v(47.5, 31) * mm});
            skLineSegment(sketch, "E60.0", {"start": v(47.5, 31) * mm, "end": v(47.5, 14) * mm});
            skLineSegment(sketch, "E61.0", {"start": v(21.5, 31) * mm, "end": v(21.5, 14) * mm});
            skLineSegment(sketch, "E62.0", {"start": v(21.5, 14) * mm, "end": v(47.5, 14) * mm});
            skArc(sketch, "E63.0", {"start": v(3, 43.4) * mm, "mid": v(2.01, 42.99) * mm, "end": v(1.6, 42) * mm});
            skArc(sketch, "E64.0", {"start": v(67.4, 42) * mm, "mid": v(66.99, 42.99) * mm, "end": v(66, 43.4) * mm});
            skArc(sketch, "E65.0", {"start": v(66, 1.6) * mm, "mid": v(66.99, 2.01) * mm, "end": v(67.4, 3) * mm});
            skArc(sketch, "E66.0", {"start": v(1.6, 3) * mm, "mid": v(2.01, 2.01) * mm, "end": v(3, 1.6) * mm});
            skCircle(sketch, "E67", {"center": v(3, 3) * mm, "radius": 3 * mm});
            skCircle(sketch, "E68", {"center": v(3, 42) * mm, "radius": 3 * mm});
            skCircle(sketch, "E69", {"center": v(66, 42) * mm, "radius": 3 * mm});
            skCircle(sketch, "E70", {"center": v(66, 3) * mm, "radius": 3 * mm});
            skSolve(sketch);
        }
        {
            var Q0;
            Q0=makeQuery(id+"F0.imprint","IMPRINT",FACE,{"disambiguationData":[TD([[makeQuery(id+"F0.imprint","IMPRINT",EDGE,{"derivedFrom":sQuery(id+"F0.wireOp",EDGE,"E55.bottom")}),-1.0]])]});
            var Q1;
            Q1=makeQuery(id+"F0.imprint","IMPRINT",FACE,{"disambiguationData":[TD([[makeQuery(id+"F0.imprint","IMPRINT",EDGE,{"derivedFrom":sQuery(id+"F0.wireOp",EDGE,"E45")}),-1.0]])]});
            var Q2;
            {var subQ0=sQuery(id+"F0.wireOp",EDGE,"E68");var subQ1=sQuery(id+"F0.wireOp",EDGE,"E13");var subQ2=makeQuery(id+"F0.imprint","INTERSECT",VERTEX,{"disambiguationData":[OD(0.0)],"derivedFrom":[subQ1,subQ0]});Q2=makeQuery(id+"F0.imprint","IMPRINT",FACE,{"disambiguationData":[TD([[makeQuery(id+"F0.imprint","IMPRINT",EDGE,{"disambiguationData":[TD([[subQ2,-1.0]])],"derivedFrom":subQ1}),1.0]])]});}
            var Q3;
            {var subQ0=sQuery(id+"F0.wireOp",EDGE,"E67");var subQ1=sQuery(id+"F0.wireOp",EDGE,"E16");var subQ2=makeQuery(id+"F0.imprint","INTERSECT",VERTEX,{"disambiguationData":[OD(0.0)],"derivedFrom":[subQ1,subQ0]});Q3=makeQuery(id+"F0.imprint","IMPRINT",FACE,{"disambiguationData":[TD([[makeQuery(id+"F0.imprint","IMPRINT",EDGE,{"disambiguationData":[TD([[subQ2,1.0]])],"derivedFrom":subQ1}),1.0]])]});}
            var Q4;
            {var subQ1=sQuery(id+"F0.wireOp",EDGE,"E10.right");var subQ6=sQuery(id+"F0.wireOp",EDGE,"E10.top");var subQ7=makeQuery(id+"F0.imprint","INTERSECT",VERTEX,{"derivedFrom":[subQ6,subQ1]});Q4=makeQuery(id+"F0.imprint","IMPRINT",FACE,{"disambiguationData":[TD([[makeQuery(id+"F0.imprint","IMPRINT",EDGE,{"disambiguationData":[TD([[subQ7,1.0]])],"derivedFrom":subQ6}),1.0]])]});}
            var Q5;
            {var subQ0=sQuery(id+"F0.wireOp",EDGE,"E70");var subQ1=sQuery(id+"F0.wireOp",EDGE,"E15");var subQ2=makeQuery(id+"F0.imprint","INTERSECT",VERTEX,{"disambiguationData":[OD(0.0)],"derivedFrom":[subQ1,subQ0]});Q5=makeQuery(id+"F0.imprint","IMPRINT",FACE,{"disambiguationData":[TD([[makeQuery(id+"F0.imprint","IMPRINT",EDGE,{"disambiguationData":[TD([[subQ2,-1.0]])],"derivedFrom":subQ1}),1.0]])]});}
            var Q6;
            {var subQ0=sQuery(id+"F0.wireOp",EDGE,"E70");var subQ1=sQuery(id+"F0.wireOp",EDGE,"E15");var subQ2=makeQuery(id+"F0.imprint","INTERSECT",VERTEX,{"disambiguationData":[OD(0.0)],"derivedFrom":[subQ1,subQ0]});Q6=makeQuery(id+"F0.imprint","IMPRINT",FACE,{"disambiguationData":[TD([[makeQuery(id+"F0.imprint","IMPRINT",EDGE,{"disambiguationData":[TD([[subQ2,1.0]])],"derivedFrom":subQ1}),1.0]])]});}
            var Q7;
            {var subQ1=sQuery(id+"F0.wireOp",EDGE,"E10.left");var subQ5=sQuery(id+"F0.wireOp",EDGE,"E10.top");var subQ6=makeQuery(id+"F0.imprint","INTERSECT",VERTEX,{"derivedFrom":[subQ5,subQ1]});Q7=makeQuery(id+"F0.imprint","IMPRINT",FACE,{"disambiguationData":[TD([[makeQuery(id+"F0.imprint","IMPRINT",EDGE,{"disambiguationData":[TD([[subQ6,-1.0]])],"derivedFrom":subQ5}),1.0]])]});}
            var Q8;
            {var subQ0=sQuery(id+"F0.wireOp",EDGE,"E67");var subQ1=sQuery(id+"F0.wireOp",EDGE,"E16");var subQ2=makeQuery(id+"F0.imprint","INTERSECT",VERTEX,{"disambiguationData":[OD(0.0)],"derivedFrom":[subQ1,subQ0]});Q8=makeQuery(id+"F0.imprint","IMPRINT",FACE,{"disambiguationData":[TD([[makeQuery(id+"F0.imprint","IMPRINT",EDGE,{"disambiguationData":[TD([[subQ2,-1.0]])],"derivedFrom":subQ1}),1.0]])]});}
            var Q9;
            {var subQ0=sQuery(id+"F0.wireOp",EDGE,"E68");var subQ1=sQuery(id+"F0.wireOp",EDGE,"E13");var subQ2=makeQuery(id+"F0.imprint","INTERSECT",VERTEX,{"disambiguationData":[OD(0.0)],"derivedFrom":[subQ1,subQ0]});Q9=makeQuery(id+"F0.imprint","IMPRINT",FACE,{"disambiguationData":[TD([[makeQuery(id+"F0.imprint","IMPRINT",EDGE,{"disambiguationData":[TD([[subQ2,1.0]])],"derivedFrom":subQ1}),1.0]])]});}
            var Q10;
            {var subQ1=sQuery(id+"F0.wireOp",EDGE,"E10.left");var subQ6=sQuery(id+"F0.wireOp",EDGE,"E10.bottom");var subQ7=makeQuery(id+"F0.imprint","INTERSECT",VERTEX,{"derivedFrom":[subQ6,subQ1]});Q10=makeQuery(id+"F0.imprint","IMPRINT",FACE,{"disambiguationData":[TD([[makeQuery(id+"F0.imprint","IMPRINT",EDGE,{"disambiguationData":[TD([[subQ7,-1.0]])],"derivedFrom":subQ6}),-1.0]])]});}
            var Q11;
            {var subQ1=sQuery(id+"F0.wireOp",EDGE,"E10.bottom");var subQ6=sQuery(id+"F0.wireOp",EDGE,"E10.right");var subQ7=makeQuery(id+"F0.imprint","INTERSECT",VERTEX,{"derivedFrom":[subQ1,subQ6]});Q11=makeQuery(id+"F0.imprint","IMPRINT",FACE,{"disambiguationData":[TD([[makeQuery(id+"F0.imprint","IMPRINT",EDGE,{"disambiguationData":[TD([[subQ7,1.0]])],"derivedFrom":subQ1}),-1.0]])]});}
            var Q12;
            {var subQ0=sQuery(id+"F0.wireOp",EDGE,"E69");var subQ1=sQuery(id+"F0.wireOp",EDGE,"E14");var subQ2=makeQuery(id+"F0.imprint","INTERSECT",VERTEX,{"disambiguationData":[OD(0.0)],"derivedFrom":[subQ1,subQ0]});Q12=makeQuery(id+"F0.imprint","IMPRINT",FACE,{"disambiguationData":[TD([[makeQuery(id+"F0.imprint","IMPRINT",EDGE,{"disambiguationData":[TD([[subQ2,1.0]])],"derivedFrom":subQ1}),1.0]])]});}
            var Q13;
            {var subQ0=sQuery(id+"F0.wireOp",EDGE,"E69");var subQ1=sQuery(id+"F0.wireOp",EDGE,"E14");var subQ2=makeQuery(id+"F0.imprint","INTERSECT",VERTEX,{"disambiguationData":[OD(0.0)],"derivedFrom":[subQ1,subQ0]});Q13=makeQuery(id+"F0.imprint","IMPRINT",FACE,{"disambiguationData":[TD([[makeQuery(id+"F0.imprint","IMPRINT",EDGE,{"disambiguationData":[TD([[subQ2,-1.0]])],"derivedFrom":subQ1}),1.0]])]});}
            var Q14;
            {var subQ0=sQuery(id+"F0.wireOp",EDGE,"E70");var subQ1=sQuery(id+"F0.wireOp",EDGE,"E7.0");var subQ2=makeQuery(id+"F0.imprint","INTERSECT",VERTEX,{"derivedFrom":[subQ1,subQ0]});Q14=makeQuery(id+"F0.imprint","IMPRINT",FACE,{"disambiguationData":[TD([[makeQuery(id+"F0.imprint","IMPRINT",EDGE,{"disambiguationData":[TD([[subQ2,-1.0]])],"derivedFrom":subQ1}),1.0]])]});}
            var Q15;
            {var subQ0=sQuery(id+"F0.wireOp",EDGE,"E68");var subQ1=sQuery(id+"F0.wireOp",EDGE,"E5.0");var subQ2=makeQuery(id+"F0.imprint","INTERSECT",VERTEX,{"derivedFrom":[subQ1,subQ0]});Q15=makeQuery(id+"F0.imprint","IMPRINT",FACE,{"disambiguationData":[TD([[makeQuery(id+"F0.imprint","IMPRINT",EDGE,{"disambiguationData":[TD([[subQ2,-1.0]])],"derivedFrom":subQ1}),-1.0]])]});}
            var Q16;
            {var subQ0=sQuery(id+"F0.wireOp",EDGE,"E67");var subQ1=sQuery(id+"F0.wireOp",EDGE,"E8.0");var subQ2=makeQuery(id+"F0.imprint","INTERSECT",VERTEX,{"derivedFrom":[subQ1,subQ0]});Q16=makeQuery(id+"F0.imprint","IMPRINT",FACE,{"disambiguationData":[TD([[makeQuery(id+"F0.imprint","IMPRINT",EDGE,{"disambiguationData":[TD([[subQ2,-1.0]])],"derivedFrom":subQ1}),1.0]])]});}
            var Q17;
            {var subQ0=sQuery(id+"F0.wireOp",EDGE,"E67");var subQ1=sQuery(id+"F0.wireOp",EDGE,"E6.0");var subQ2=makeQuery(id+"F0.imprint","INTERSECT",VERTEX,{"derivedFrom":[subQ1,subQ0]});Q17=makeQuery(id+"F0.imprint","IMPRINT",FACE,{"disambiguationData":[TD([[makeQuery(id+"F0.imprint","IMPRINT",EDGE,{"disambiguationData":[TD([[subQ2,-1.0]])],"derivedFrom":subQ1}),-1.0]])]});}
            var Q18;
            {var subQ5=sQuery(id+"F0.wireOp",EDGE,"E65.0");Q18=makeQuery(id+"F0.imprint","IMPRINT",FACE,{"disambiguationData":[TD([[makeQuery(id+"F0.imprint","IMPRINT",EDGE,{"derivedFrom":subQ5}),1.0]])]});}
            var Q19;
            {var subQ10=sQuery(id+"F0.wireOp",EDGE,"E64.0");Q19=makeQuery(id+"F0.imprint","IMPRINT",FACE,{"disambiguationData":[TD([[makeQuery(id+"F0.imprint","IMPRINT",EDGE,{"derivedFrom":subQ10}),1.0]])]});}
            var Q20;
            {var subQ5=sQuery(id+"F0.wireOp",EDGE,"E66.0");Q20=makeQuery(id+"F0.imprint","IMPRINT",FACE,{"disambiguationData":[TD([[makeQuery(id+"F0.imprint","IMPRINT",EDGE,{"derivedFrom":subQ5}),1.0]])]});}
            var Q21;
            {var subQ6=sQuery(id+"F0.wireOp",EDGE,"E63.0");Q21=makeQuery(id+"F0.imprint","IMPRINT",FACE,{"disambiguationData":[TD([[makeQuery(id+"F0.imprint","IMPRINT",EDGE,{"derivedFrom":subQ6}),1.0]])]});}
            extrude(context, id + "F1", {"entities" : qUnion([Q0, Q1, Q2, Q3, Q4, Q5, Q6, Q7, Q8, Q9, Q10, Q11, Q12, Q13, Q14, Q15, Q16, Q17, Q18, Q19, Q20, Q21]), "depth" : 2 * mm});
        }
        {
            var Q0;
            Q0=makeQuery(id+"F0.imprint","IMPRINT",FACE,{"disambiguationData":[TD([[makeQuery(id+"F0.imprint","IMPRINT",EDGE,{"derivedFrom":sQuery(id+"F0.wireOp",EDGE,"E55.bottom")}),1.0]])]});
            extrude(context, id + "F2", {"entities" : qUnion([Q0]), "operationType" : NewBodyOperationType.ADD, "depth" : 4 * mm});
        }
        {
            var Q0;
            Q0=makeQuery(id+"F0.imprint","IMPRINT",FACE,{"disambiguationData":[TD([[makeQuery(id+"F0.imprint","IMPRINT",EDGE,{"derivedFrom":sQuery(id+"F0.wireOp",EDGE,"E0.bottom")}),1.0]])]});
            var Q1;
            {var subQ4=sQuery(id+"F0.wireOp",EDGE,"E66.0");Q1=makeQuery(id+"F0.imprint","IMPRINT",FACE,{"disambiguationData":[TD([[makeQuery(id+"F0.imprint","IMPRINT",EDGE,{"derivedFrom":subQ4}),-1.0]])]});}
            var Q2;
            {var subQ0=sQuery(id+"F0.wireOp",EDGE,"E0.left");Q2=makeQuery(id+"F0.imprint","IMPRINT",FACE,{"disambiguationData":[TD([[makeQuery(id+"F0.imprint","IMPRINT",EDGE,{"derivedFrom":subQ0}),-1.0]])]});}
            var Q3;
            {var subQ4=sQuery(id+"F0.wireOp",EDGE,"E63.0");Q3=makeQuery(id+"F0.imprint","IMPRINT",FACE,{"disambiguationData":[TD([[makeQuery(id+"F0.imprint","IMPRINT",EDGE,{"derivedFrom":subQ4}),-1.0]])]});}
            var Q4;
            {var subQ0=sQuery(id+"F0.wireOp",EDGE,"E0.top");Q4=makeQuery(id+"F0.imprint","IMPRINT",FACE,{"disambiguationData":[TD([[makeQuery(id+"F0.imprint","IMPRINT",EDGE,{"derivedFrom":subQ0}),-1.0]])]});}
            var Q5;
            {var subQ0=sQuery(id+"F0.wireOp",EDGE,"E0.right");Q5=makeQuery(id+"F0.imprint","IMPRINT",FACE,{"disambiguationData":[TD([[makeQuery(id+"F0.imprint","IMPRINT",EDGE,{"derivedFrom":subQ0}),1.0]])]});}
            var Q6;
            {var subQ3=sQuery(id+"F0.wireOp",EDGE,"E64.0");Q6=makeQuery(id+"F0.imprint","IMPRINT",FACE,{"disambiguationData":[TD([[makeQuery(id+"F0.imprint","IMPRINT",EDGE,{"derivedFrom":subQ3}),-1.0]])]});}
            var Q7;
            {var subQ4=sQuery(id+"F0.wireOp",EDGE,"E65.0");Q7=makeQuery(id+"F0.imprint","IMPRINT",FACE,{"disambiguationData":[TD([[makeQuery(id+"F0.imprint","IMPRINT",EDGE,{"derivedFrom":subQ4}),-1.0]])]});}
            extrude(context, id + "F3", {"entities" : qUnion([Q0, Q1, Q2, Q3, Q4, Q5, Q6, Q7]), "operationType" : NewBodyOperationType.ADD, "depth" : 15 * mm});
        }
        {
            var Q0;
            Q0=makeQuery(id+"F3.opExtrude","CAP_FACE",FACE,{"disambiguationData":[OSD([sQuery(id+"F0.wireOp",EDGE,"E0.bottom"),sQuery(id+"F0.wireOp",EDGE,"E0.top"),sQuery(id+"F0.wireOp",EDGE,"E0.left"),sQuery(id+"F0.wireOp",EDGE,"E0.right"),sQuery(id+"F0.wireOp",EDGE,"E5.0"),sQuery(id+"F0.wireOp",EDGE,"E6.0"),sQuery(id+"F0.wireOp",EDGE,"E7.0"),sQuery(id+"F0.wireOp",EDGE,"E8.0"),sQuery(id+"F0.wireOp",EDGE,"E63.0"),sQuery(id+"F0.wireOp",EDGE,"E64.0"),sQuery(id+"F0.wireOp",EDGE,"E65.0"),sQuery(id+"F0.wireOp",EDGE,"E66.0"),sQuery(id+"F0.wireOp",EDGE,"E67"),sQuery(id+"F0.wireOp",EDGE,"E68"),sQuery(id+"F0.wireOp",EDGE,"E69"),sQuery(id+"F0.wireOp",EDGE,"E70")])],"isStart":false});
            var sketch = newSketch(context, id + "F4", { "sketchPlane" : qUnion([Q0])});
            skLineSegment(sketch, "E71.0.0", {"start": v(3, 0) * mm, "end": v(66, 0) * mm});
            skArc(sketch, "E71.0.1", {"start": v(66, 0) * mm, "mid": v(68.12, 0.88) * mm, "end": v(69, 3) * mm});
            skLineSegment(sketch, "E71.0.2", {"start": v(69, 3) * mm, "end": v(69, 42) * mm});
            skArc(sketch, "E71.0.3", {"start": v(69, 42) * mm, "mid": v(68.12, 44.12) * mm, "end": v(66, 45) * mm});
            skLineSegment(sketch, "E71.0.4", {"start": v(66, 45) * mm, "end": v(3, 45) * mm});
            skArc(sketch, "E71.0.5", {"start": v(3, 45) * mm, "mid": v(0.88, 44.12) * mm, "end": v(0, 42) * mm});
            skLineSegment(sketch, "E71.0.6", {"start": v(0, 42) * mm, "end": v(0, 3) * mm});
            skArc(sketch, "E71.0.7", {"start": v(0, 3) * mm, "mid": v(0.88, 0.88) * mm, "end": v(3, 0) * mm});
            skLineSegment(sketch, "E72", {"start": v(57, 53.28) * mm, "end": v(57, -12.37) * mm, "construction": true});
            skLineSegment(sketch, "E73", {"start": v(12, 52.9) * mm, "end": v(12, -13.89) * mm, "construction": true});
            skArc(sketch, "E74", {"start": v(64, 45) * mm, "mid": v(57, 52) * mm, "end": v(50, 45) * mm});
            skArc(sketch, "E75", {"start": v(19, 45) * mm, "mid": v(12, 52) * mm, "end": v(5, 45) * mm});
            skArc(sketch, "E76", {"start": v(5, 0) * mm, "mid": v(12, -7) * mm, "end": v(19, 0) * mm});
            skArc(sketch, "E77", {"start": v(64, 0) * mm, "mid": v(57, -7) * mm, "end": v(50, 0) * mm});
            skSolve(sketch);
        }
        {
            var Q0;
            {var subQ0=sQuery(id+"F4.wireOp",EDGE,"E74");Q0=makeQuery(id+"F4.imprint","IMPRINT",FACE,{"disambiguationData":[TD([[makeQuery(id+"F4.imprint","IMPRINT",EDGE,{"derivedFrom":subQ0}),1.0]])]});}
            var Q1;
            {var subQ0=sQuery(id+"F4.wireOp",EDGE,"E77");Q1=makeQuery(id+"F4.imprint","IMPRINT",FACE,{"disambiguationData":[TD([[makeQuery(id+"F4.imprint","IMPRINT",EDGE,{"derivedFrom":subQ0}),-1.0]])]});}
            var Q2;
            {var subQ0=sQuery(id+"F4.wireOp",EDGE,"E76");Q2=makeQuery(id+"F4.imprint","IMPRINT",FACE,{"disambiguationData":[TD([[makeQuery(id+"F4.imprint","IMPRINT",EDGE,{"derivedFrom":subQ0}),1.0]])]});}
            var Q3;
            {var subQ0=sQuery(id+"F4.wireOp",EDGE,"E75");Q3=makeQuery(id+"F4.imprint","IMPRINT",FACE,{"disambiguationData":[TD([[makeQuery(id+"F4.imprint","IMPRINT",EDGE,{"derivedFrom":subQ0}),1.0]])]});}
            extrude(context, id + "F5", {"entities" : qUnion([Q0, Q1, Q2, Q3]), "operationType" : NewBodyOperationType.ADD, "oppositeDirection" : true, "depth" : 15 * mm});
        }
        {
            var Q0;
            Q0=makeQuery(id+"F3.opExtrude","CAP_EDGE",EDGE,{"disambiguationData":[OSD([sQuery(id+"F0.wireOp",EDGE,"E0.top")])],"isStart":true});
            var Q1;
            Q1=makeQuery(id+"F3.opExtrude","CAP_EDGE",EDGE,{"disambiguationData":[OSD([sQuery(id+"F0.wireOp",EDGE,"E1.filletArc")])],"isStart":true});
            var Q2;
            Q2=makeQuery(id+"F5.opExtrude","CAP_EDGE",EDGE,{"disambiguationData":[OSD([sQuery(id+"F4.wireOp",EDGE,"E75")])],"isStart":false});
            var Q3;
            Q3=makeQuery(id+"F5.opExtrude","CAP_EDGE",EDGE,{"disambiguationData":[OSD([sQuery(id+"F4.wireOp",EDGE,"E74")])],"isStart":false});
            var Q4;
            Q4=makeQuery(id+"F5.opExtrude","CAP_EDGE",EDGE,{"disambiguationData":[OSD([sQuery(id+"F4.wireOp",EDGE,"E77")])],"isStart":false});
            var Q5;
            {var subQ0=sQuery(id+"F4.wireOp",EDGE,"E76");var subQ1=sQuery(id+"F4.wireOp",EDGE,"E71.0.4");var subQ2=sQuery(id+"F4.wireOp",EDGE,"E77");var subQ3=sQuery(id+"F4.wireOp",EDGE,"E71.0.0");var subQ4=sQuery(id+"F0.wireOp",EDGE,"E66.0");var subQ5=sQuery(id+"F0.wireOp",EDGE,"E65.0");var subQ6=sQuery(id+"F0.wireOp",EDGE,"E64.0");var subQ7=sQuery(id+"F0.wireOp",EDGE,"E63.0");var subQ8=sQuery(id+"F0.wireOp",EDGE,"E8.0");var subQ9=sQuery(id+"F0.wireOp",EDGE,"E7.0");var subQ10=sQuery(id+"F0.wireOp",EDGE,"E6.0");var subQ11=sQuery(id+"F0.wireOp",EDGE,"E5.0");var subQ12=sQuery(id+"F0.wireOp",EDGE,"E0.bottom");var subQ13=sQuery(id+"F0.wireOp",EDGE,"E55.right");var subQ14=sQuery(id+"F0.wireOp",EDGE,"E55.left");var subQ15=sQuery(id+"F0.wireOp",EDGE,"E55.top");var subQ16=sQuery(id+"F0.wireOp",EDGE,"E55.bottom");var subQ17=sQuery(id+"F0.wireOp",EDGE,"E62.0");var subQ18=sQuery(id+"F0.wireOp",EDGE,"E61.0");var subQ19=sQuery(id+"F0.wireOp",EDGE,"E60.0");var subQ20=sQuery(id+"F0.wireOp",EDGE,"E59.0");Q5=makeQuery(id+"F5.boolean.opBoolean","SPLIT",EDGE,{"disambiguationData":[TD([makeQuery(id+"F1.opExtrude","CAP_FACE",FACE,{"disambiguationData":[OSD([subQ11,subQ10,subQ9,subQ8,sQuery(id+"F0.wireOp",EDGE,"E45"),sQuery(id+"F0.wireOp",EDGE,"E46"),sQuery(id+"F0.wireOp",EDGE,"E47"),sQuery(id+"F0.wireOp",EDGE,"E48"),sQuery(id+"F0.wireOp",EDGE,"E49"),sQuery(id+"F0.wireOp",EDGE,"E50"),sQuery(id+"F0.wireOp",EDGE,"E51"),sQuery(id+"F0.wireOp",EDGE,"E52"),sQuery(id+"F0.wireOp",EDGE,"E53"),sQuery(id+"F0.wireOp",EDGE,"E54"),subQ20,subQ19,subQ18,subQ17,subQ7,subQ6,subQ5,subQ4])],"isStart":true}),makeQuery(id+"F1.opExtrude","CAP_FACE",FACE,{"disambiguationData":[OSD([subQ16,subQ15,subQ14,subQ13,sQuery(id+"F0.wireOp",EDGE,"E58.bottom"),sQuery(id+"F0.wireOp",EDGE,"E58.top"),sQuery(id+"F0.wireOp",EDGE,"E58.left"),sQuery(id+"F0.wireOp",EDGE,"E58.right")])],"isStart":true}),makeQuery(id+"F2.opExtrude","CAP_FACE",FACE,{"disambiguationData":[OSD([subQ16,subQ15,subQ14,subQ13,subQ20,subQ19,subQ18,subQ17])],"isStart":true}),makeQuery(id+"F3.opExtrude","SWEPT_FACE",FACE,{"disambiguationData":[OSD([subQ12])]}),makeQuery(id+"F3.opExtrude","CAP_FACE",FACE,{"disambiguationData":[OSD([subQ12,sQuery(id+"F0.wireOp",EDGE,"E0.top"),sQuery(id+"F0.wireOp",EDGE,"E0.left"),sQuery(id+"F0.wireOp",EDGE,"E0.right"),subQ11,subQ10,subQ9,subQ8,subQ7,subQ6,subQ5,subQ4,sQuery(id+"F0.wireOp",EDGE,"E67"),sQuery(id+"F0.wireOp",EDGE,"E68"),sQuery(id+"F0.wireOp",EDGE,"E69"),sQuery(id+"F0.wireOp",EDGE,"E70")])],"isStart":true}),makeQuery(id+"F5.opExtrude","CAP_FACE",FACE,{"disambiguationData":[OSD([subQ3,subQ0])],"isStart":false}),makeQuery(id+"F5.opExtrude","CAP_FACE",FACE,{"disambiguationData":[OSD([subQ3,subQ2])],"isStart":false}),makeQuery(id+"F5.opExtrude","CAP_FACE",FACE,{"disambiguationData":[OSD([subQ1,sQuery(id+"F4.wireOp",EDGE,"E75")])],"isStart":false}),makeQuery(id+"F5.opExtrude","CAP_FACE",FACE,{"disambiguationData":[OSD([subQ1,sQuery(id+"F4.wireOp",EDGE,"E74")])],"isStart":false}),makeQuery(id+"F5.opExtrude","SWEPT_FACE",FACE,{"disambiguationData":[OSD([subQ0])]}),makeQuery(id+"F5.opExtrude","SWEPT_FACE",FACE,{"disambiguationData":[OSD([subQ2])]})])],"derivedFrom":makeQuery(id+"F3.opExtrude","CAP_EDGE",EDGE,{"disambiguationData":[OSD([subQ12])],"isStart":true})});}
            var Q6;
            Q6=makeQuery(id+"F5.opExtrude","CAP_EDGE",EDGE,{"disambiguationData":[OSD([sQuery(id+"F4.wireOp",EDGE,"E76")])],"isStart":false});
            fillet(context, id + "F6", {"entities" : qUnion([Q0, Q1, Q2, Q3, Q4, Q5, Q6]), "radius" : 3 * mm, "tangentPropagation" : true, "allowEdgeOverflow" : false});
        }
        {
            var Q0;
            Q0=makeQuery(id+"F1.opExtrude","CAP_EDGE",EDGE,{"disambiguationData":[OSD([sQuery(id+"F0.wireOp",EDGE,"E53")])],"isStart":true});
            var Q1;
            Q1=makeQuery(id+"F1.opExtrude","CAP_EDGE",EDGE,{"disambiguationData":[OSD([sQuery(id+"F0.wireOp",EDGE,"E54")])],"isStart":true});
            var Q2;
            Q2=makeQuery(id+"F1.opExtrude","CAP_EDGE",EDGE,{"disambiguationData":[OSD([sQuery(id+"F0.wireOp",EDGE,"E52")])],"isStart":true});
            var Q3;
            Q3=makeQuery(id+"F1.opExtrude","CAP_EDGE",EDGE,{"disambiguationData":[OSD([sQuery(id+"F0.wireOp",EDGE,"E51")])],"isStart":true});
            var Q4;
            Q4=makeQuery(id+"F1.opExtrude","CAP_EDGE",EDGE,{"disambiguationData":[OSD([sQuery(id+"F0.wireOp",EDGE,"E50")])],"isStart":true});
            var Q5;
            Q5=makeQuery(id+"F1.opExtrude","CAP_EDGE",EDGE,{"disambiguationData":[OSD([sQuery(id+"F0.wireOp",EDGE,"E58.top")])],"isStart":true});
            var Q6;
            Q6=makeQuery(id+"F1.opExtrude","CAP_EDGE",EDGE,{"disambiguationData":[OSD([sQuery(id+"F0.wireOp",EDGE,"E58.right")])],"isStart":true});
            var Q7;
            Q7=makeQuery(id+"F1.opExtrude","CAP_EDGE",EDGE,{"disambiguationData":[OSD([sQuery(id+"F0.wireOp",EDGE,"E58.bottom")])],"isStart":true});
            var Q8;
            Q8=makeQuery(id+"F1.opExtrude","CAP_EDGE",EDGE,{"disambiguationData":[OSD([sQuery(id+"F0.wireOp",EDGE,"E58.left")])],"isStart":true});
            var Q9;
            Q9=makeQuery(id+"F1.opExtrude","CAP_EDGE",EDGE,{"disambiguationData":[OSD([sQuery(id+"F0.wireOp",EDGE,"E45")])],"isStart":true});
            var Q10;
            Q10=makeQuery(id+"F1.opExtrude","CAP_EDGE",EDGE,{"disambiguationData":[OSD([sQuery(id+"F0.wireOp",EDGE,"E46")])],"isStart":true});
            var Q11;
            Q11=makeQuery(id+"F1.opExtrude","CAP_EDGE",EDGE,{"disambiguationData":[OSD([sQuery(id+"F0.wireOp",EDGE,"E47")])],"isStart":true});
            var Q12;
            Q12=makeQuery(id+"F1.opExtrude","CAP_EDGE",EDGE,{"disambiguationData":[OSD([sQuery(id+"F0.wireOp",EDGE,"E48")])],"isStart":true});
            var Q13;
            Q13=makeQuery(id+"F1.opExtrude","CAP_EDGE",EDGE,{"disambiguationData":[OSD([sQuery(id+"F0.wireOp",EDGE,"E49")])],"isStart":true});
            chamfer(context, id + "F7", {"entities" : qUnion([Q0, Q1, Q2, Q3, Q4, Q5, Q6, Q7, Q8, Q9, Q10, Q11, Q12, Q13]), "width" : .5 * mm, "tangentPropagation" : true});
        }
        {
            var Q0;
            Q0=makeQuery(id+"F2.opExtrude","CAP_EDGE",EDGE,{"disambiguationData":[OSD([sQuery(id+"F0.wireOp",EDGE,"E61.0")])],"isStart":false});
            var Q1;
            Q1=makeQuery(id+"F2.opExtrude","CAP_EDGE",EDGE,{"disambiguationData":[OSD([sQuery(id+"F0.wireOp",EDGE,"E59.0")])],"isStart":false});
            var Q2;
            Q2=makeQuery(id+"F2.opExtrude","CAP_EDGE",EDGE,{"disambiguationData":[OSD([sQuery(id+"F0.wireOp",EDGE,"E60.0")])],"isStart":false});
            var Q3;
            Q3=makeQuery(id+"F2.opExtrude","CAP_EDGE",EDGE,{"disambiguationData":[OSD([sQuery(id+"F0.wireOp",EDGE,"E62.0")])],"isStart":false});
            chamfer(context, id + "F8", {"entities" : qUnion([Q0, Q1, Q2, Q3]), "width" : 2 * mm, "tangentPropagation" : true});
        }
        {
            var Q0;
            Q0=qCreatedBy(makeId("Top.planeOp"),FACE);
            var sketch = newSketch(context, id + "F9", { "sketchPlane" : qUnion([Q0])});
            skLineSegment(sketch, "E78.bottom", {"start": v(-71, 19.43) * mm, "end": v(-8, 19.43) * mm});
            skLineSegment(sketch, "E78.top", {"start": v(-71, 64.43) * mm, "end": v(-8, 64.43) * mm});
            skLineSegment(sketch, "E78.left", {"start": v(-74, 22.43) * mm, "end": v(-74, 61.43) * mm});
            skLineSegment(sketch, "E78.right", {"start": v(-5, 22.43) * mm, "end": v(-5, 61.43) * mm});
            skArc(sketch, "E79.filletArc", {"start": v(-71, 64.43) * mm, "mid": v(-73.13, 63.55) * mm, "end": v(-74, 61.43) * mm});
            skArc(sketch, "E80.filletArc", {"start": v(-5, 61.43) * mm, "mid": v(-5.89, 63.55) * mm, "end": v(-8, 64.43) * mm});
            skArc(sketch, "E81.filletArc", {"start": v(-74, 22.43) * mm, "mid": v(-73.13, 20.31) * mm, "end": v(-71, 19.43) * mm});
            skArc(sketch, "E82.filletArc", {"start": v(-8, 19.43) * mm, "mid": v(-5.89, 20.31) * mm, "end": v(-5, 22.43) * mm});
            skLineSegment(sketch, "E83.0", {"start": v(-71, 62.83) * mm, "end": v(-6.88, 62.83) * mm});
            skLineSegment(sketch, "E84.0", {"start": v(-72.4, 22.43) * mm, "end": v(-72.4, 61.43) * mm});
            skLineSegment(sketch, "E85.0", {"start": v(-6.6, 22.43) * mm, "end": v(-6.6, 61.43) * mm});
            skLineSegment(sketch, "E86.0", {"start": v(-71, 21.03) * mm, "end": v(-6.88, 21.03) * mm});
            skArc(sketch, "E87.0", {"start": v(-71, 62.83) * mm, "mid": v(-72, 62.42) * mm, "end": v(-72.4, 61.43) * mm});
            skArc(sketch, "E88.0", {"start": v(-6.6, 61.43) * mm, "mid": v(-7.02, 62.42) * mm, "end": v(-8, 62.83) * mm});
            skArc(sketch, "E89.0", {"start": v(-8, 21.03) * mm, "mid": v(-7.02, 21.44) * mm, "end": v(-6.6, 22.43) * mm});
            skArc(sketch, "E90.0", {"start": v(-72.4, 22.43) * mm, "mid": v(-72, 21.44) * mm, "end": v(-71, 21.03) * mm});
            skLineSegment(sketch, "E91", {"start": v(-17, 72.06) * mm, "end": v(-17, -23.84) * mm, "construction": true});
            skLineSegment(sketch, "E92", {"start": v(-62, -15.69) * mm, "end": v(-62, 74.59) * mm, "construction": true});
            skArc(sketch, "E93", {"start": v(-69, 64.43) * mm, "mid": v(-62, 71.43) * mm, "end": v(-55, 64.43) * mm});
            skArc(sketch, "E94", {"start": v(-24, 64.43) * mm, "mid": v(-17, 71.43) * mm, "end": v(-10, 64.43) * mm});
            skArc(sketch, "E95", {"start": v(-55, 19.43) * mm, "mid": v(-62, 12.43) * mm, "end": v(-69, 19.43) * mm});
            skArc(sketch, "E96", {"start": v(-24, 19.43) * mm, "mid": v(-17, 12.43) * mm, "end": v(-10, 19.43) * mm});
            skSolve(sketch);
        }
        {
            var Q0;
            Q0=makeQuery(id+"F9.imprint","IMPRINT",FACE,{"disambiguationData":[TD([[makeQuery(id+"F9.imprint","IMPRINT",EDGE,{"derivedFrom":sQuery(id+"F9.wireOp",EDGE,"E84.0")}),-1.0]])]});
            extrude(context, id + "F10", {"entities" : qUnion([Q0]), "depth" : 2 * mm});
        }
        {
            var Q0;
            {var subQ0=sQuery(id+"F9.wireOp",EDGE,"E95");Q0=makeQuery(id+"F9.imprint","IMPRINT",FACE,{"disambiguationData":[TD([[makeQuery(id+"F9.imprint","IMPRINT",EDGE,{"derivedFrom":subQ0}),-1.0]])]});}
            var Q1;
            Q1=makeQuery(id+"F9.imprint","IMPRINT",FACE,{"disambiguationData":[TD([[makeQuery(id+"F9.imprint","IMPRINT",EDGE,{"derivedFrom":sQuery(id+"F9.wireOp",EDGE,"E78.left")}),-1.0]])]});
            var Q2;
            {var subQ0=sQuery(id+"F9.wireOp",EDGE,"E93");Q2=makeQuery(id+"F9.imprint","IMPRINT",FACE,{"disambiguationData":[TD([[makeQuery(id+"F9.imprint","IMPRINT",EDGE,{"derivedFrom":subQ0}),-1.0]])]});}
            var Q3;
            {var subQ0=sQuery(id+"F9.wireOp",EDGE,"E94");Q3=makeQuery(id+"F9.imprint","IMPRINT",FACE,{"disambiguationData":[TD([[makeQuery(id+"F9.imprint","IMPRINT",EDGE,{"derivedFrom":subQ0}),-1.0]])]});}
            var Q4;
            {var subQ0=sQuery(id+"F9.wireOp",EDGE,"E96");Q4=makeQuery(id+"F9.imprint","IMPRINT",FACE,{"disambiguationData":[TD([[makeQuery(id+"F9.imprint","IMPRINT",EDGE,{"derivedFrom":subQ0}),1.0]])]});}
            extrude(context, id + "F11", {"entities" : qUnion([Q0, Q1, Q2, Q3, Q4]), "operationType" : NewBodyOperationType.ADD, "depth" : 15 * mm});
        }
        {
            var Q0;
            {var subQ0=sQuery(id+"F9.wireOp",EDGE,"E90.0");var subQ1=sQuery(id+"F9.wireOp",EDGE,"E89.0");var subQ2=sQuery(id+"F9.wireOp",EDGE,"E88.0");var subQ3=sQuery(id+"F9.wireOp",EDGE,"E87.0");var subQ4=sQuery(id+"F9.wireOp",EDGE,"E86.0");var subQ5=sQuery(id+"F9.wireOp",EDGE,"E85.0");var subQ6=sQuery(id+"F9.wireOp",EDGE,"E84.0");var subQ7=sQuery(id+"F9.wireOp",EDGE,"E83.0");Q0=makeQuery(id+"F11.boolean.opBoolean","MERGE",FACE,{"derivedFrom":[makeQuery(id+"F10.opExtrude","CAP_FACE",FACE,{"disambiguationData":[OSD([subQ7,subQ6,subQ5,subQ4,subQ3,subQ2,subQ1,subQ0])],"isStart":true}),makeQuery(id+"F11.opExtrude","CAP_FACE",FACE,{"disambiguationData":[OSD([sQuery(id+"F9.wireOp",EDGE,"E78.bottom"),sQuery(id+"F9.wireOp",EDGE,"E78.top"),sQuery(id+"F9.wireOp",EDGE,"E78.left"),sQuery(id+"F9.wireOp",EDGE,"E78.right"),sQuery(id+"F9.wireOp",EDGE,"E79.filletArc"),sQuery(id+"F9.wireOp",EDGE,"E80.filletArc"),sQuery(id+"F9.wireOp",EDGE,"E81.filletArc"),sQuery(id+"F9.wireOp",EDGE,"E82.filletArc"),subQ7,subQ6,subQ5,subQ4,subQ3,subQ2,subQ1,subQ0,sQuery(id+"F9.wireOp",EDGE,"E93"),sQuery(id+"F9.wireOp",EDGE,"E94"),sQuery(id+"F9.wireOp",EDGE,"E95"),sQuery(id+"F9.wireOp",EDGE,"E96")])],"isStart":true})]});}
            fillet(context, id + "F12", {"entities" : qUnion([Q0]), "radius" : 3 * mm, "tangentPropagation" : true, "allowEdgeOverflow" : false});
        }
        {
            var Q0;
            Q0=makeQuery(id+"F11.opExtrude","CAP_FACE",FACE,{"disambiguationData":[OSD([sQuery(id+"F9.wireOp",EDGE,"E78.bottom"),sQuery(id+"F9.wireOp",EDGE,"E78.top"),sQuery(id+"F9.wireOp",EDGE,"E78.left"),sQuery(id+"F9.wireOp",EDGE,"E78.right"),sQuery(id+"F9.wireOp",EDGE,"E79.filletArc"),sQuery(id+"F9.wireOp",EDGE,"E80.filletArc"),sQuery(id+"F9.wireOp",EDGE,"E81.filletArc"),sQuery(id+"F9.wireOp",EDGE,"E82.filletArc"),sQuery(id+"F9.wireOp",EDGE,"E83.0"),sQuery(id+"F9.wireOp",EDGE,"E84.0"),sQuery(id+"F9.wireOp",EDGE,"E85.0"),sQuery(id+"F9.wireOp",EDGE,"E86.0"),sQuery(id+"F9.wireOp",EDGE,"E87.0"),sQuery(id+"F9.wireOp",EDGE,"E88.0"),sQuery(id+"F9.wireOp",EDGE,"E89.0"),sQuery(id+"F9.wireOp",EDGE,"E90.0"),sQuery(id+"F9.wireOp",EDGE,"E93"),sQuery(id+"F9.wireOp",EDGE,"E94"),sQuery(id+"F9.wireOp",EDGE,"E95"),sQuery(id+"F9.wireOp",EDGE,"E96")])],"isStart":false});
            var sketch = newSketch(context, id + "F13", { "sketchPlane" : qUnion([Q0])});
            skArc(sketch, "E97.0.0", {"start": v(-69, 19.43) * mm, "mid": v(-62, 12.43) * mm, "end": v(-55, 19.43) * mm});
            skLineSegment(sketch, "E97.0.1", {"start": v(-55, 19.43) * mm, "end": v(-24, 19.43) * mm});
            skArc(sketch, "E97.0.2", {"start": v(-24, 19.43) * mm, "mid": v(-17, 12.43) * mm, "end": v(-10, 19.43) * mm});
            skLineSegment(sketch, "E97.0.3", {"start": v(-10, 19.43) * mm, "end": v(-8, 19.43) * mm});
            skArc(sketch, "E97.0.4", {"start": v(-8, 19.43) * mm, "mid": v(-5.89, 20.31) * mm, "end": v(-5, 22.43) * mm});
            skLineSegment(sketch, "E97.0.5", {"start": v(-5, 22.43) * mm, "end": v(-5, 61.43) * mm});
            skArc(sketch, "E97.0.6", {"start": v(-5, 61.43) * mm, "mid": v(-5.89, 63.55) * mm, "end": v(-8, 64.43) * mm});
            skLineSegment(sketch, "E97.0.7", {"start": v(-8, 64.43) * mm, "end": v(-10, 64.43) * mm});
            skArc(sketch, "E97.0.8", {"start": v(-10, 64.43) * mm, "mid": v(-17, 71.43) * mm, "end": v(-24, 64.43) * mm});
            skLineSegment(sketch, "E97.0.9", {"start": v(-24, 64.43) * mm, "end": v(-55, 64.43) * mm});
            skArc(sketch, "E97.0.10", {"start": v(-55, 64.43) * mm, "mid": v(-62, 71.43) * mm, "end": v(-69, 64.43) * mm});
            skLineSegment(sketch, "E97.0.11", {"start": v(-69, 64.43) * mm, "end": v(-71, 64.43) * mm});
            skArc(sketch, "E97.0.12", {"start": v(-71, 64.43) * mm, "mid": v(-73.13, 63.55) * mm, "end": v(-74, 61.43) * mm});
            skLineSegment(sketch, "E97.0.13", {"start": v(-74, 61.43) * mm, "end": v(-74, 22.43) * mm});
            skArc(sketch, "E97.0.14", {"start": v(-74, 22.43) * mm, "mid": v(-73.13, 20.31) * mm, "end": v(-71, 19.43) * mm});
            skLineSegment(sketch, "E97.0.15", {"start": v(-71, 19.43) * mm, "end": v(-69, 19.43) * mm});
            skLineSegment(sketch, "E98.0.0", {"start": v(3, 0) * mm, "end": v(5, 0) * mm});
            skArc(sketch, "E98.0.1", {"start": v(5, 0) * mm, "mid": v(12, -7) * mm, "end": v(19, 0) * mm});
            skLineSegment(sketch, "E98.0.2", {"start": v(19, 0) * mm, "end": v(50, 0) * mm});
            skArc(sketch, "E98.0.3", {"start": v(50, 0) * mm, "mid": v(57, -7) * mm, "end": v(64, 0) * mm});
            skLineSegment(sketch, "E98.0.4", {"start": v(64, 0) * mm, "end": v(66, 0) * mm});
            skArc(sketch, "E98.0.5", {"start": v(66, 0) * mm, "mid": v(68.12, 0.88) * mm, "end": v(69, 3) * mm});
            skLineSegment(sketch, "E98.0.6", {"start": v(69, 3) * mm, "end": v(69, 42) * mm});
            skArc(sketch, "E98.0.7", {"start": v(69, 42) * mm, "mid": v(68.12, 44.12) * mm, "end": v(66, 45) * mm});
            skLineSegment(sketch, "E98.0.8", {"start": v(66, 45) * mm, "end": v(64, 45) * mm});
            skArc(sketch, "E98.0.9", {"start": v(64, 45) * mm, "mid": v(57, 52) * mm, "end": v(50, 45) * mm});
            skLineSegment(sketch, "E98.0.10", {"start": v(50, 45) * mm, "end": v(19, 45) * mm});
            skArc(sketch, "E98.0.11", {"start": v(19, 45) * mm, "mid": v(12, 52) * mm, "end": v(5, 45) * mm});
            skLineSegment(sketch, "E98.0.12", {"start": v(5, 45) * mm, "end": v(3, 45) * mm});
            skArc(sketch, "E98.0.13", {"start": v(3, 45) * mm, "mid": v(0.88, 44.12) * mm, "end": v(0, 42) * mm});
            skLineSegment(sketch, "E98.0.14", {"start": v(0, 42) * mm, "end": v(0, 3) * mm});
            skArc(sketch, "E98.0.15", {"start": v(0, 3) * mm, "mid": v(0.88, 0.88) * mm, "end": v(3, 0) * mm});
            skCircle(sketch, "E99", {"center": v(-17, 66.93) * mm, "radius": 2.5 * mm});
            skCircle(sketch, "E100", {"center": v(-62, 16.93) * mm, "radius": 2.5 * mm});
            skCircle(sketch, "E101", {"center": v(-62, 66.93) * mm, "radius": 2.7 * mm});
            skCircle(sketch, "E102", {"center": v(-17, 16.93) * mm, "radius": 2.7 * mm});
            skCircle(sketch, "E103", {"center": v(12, 47.5) * mm, "radius": 2.7 * mm});
            skCircle(sketch, "E104", {"center": v(57, 47.5) * mm, "radius": 2.5 * mm});
            skCircle(sketch, "E105", {"center": v(12, -2.5) * mm, "radius": 2.5 * mm});
            skCircle(sketch, "E106", {"center": v(57, -2.5) * mm, "radius": 2.7 * mm});
            skSolve(sketch);
        }
        {
            var Q0;
            Q0=makeQuery(id+"F13.imprint","IMPRINT",FACE,{"disambiguationData":[TD([[makeQuery(id+"F13.imprint","IMPRINT",EDGE,{"derivedFrom":sQuery(id+"F13.wireOp",EDGE,"E101")}),1.0]])]});
            var Q1;
            Q1=makeQuery(id+"F13.imprint","IMPRINT",FACE,{"disambiguationData":[TD([[makeQuery(id+"F13.imprint","IMPRINT",EDGE,{"derivedFrom":sQuery(id+"F13.wireOp",EDGE,"E102")}),1.0]])]});
            var Q2;
            Q2=makeQuery(id+"F13.imprint","IMPRINT",FACE,{"disambiguationData":[TD([[makeQuery(id+"F13.imprint","IMPRINT",EDGE,{"derivedFrom":sQuery(id+"F13.wireOp",EDGE,"E103")}),1.0]])]});
            var Q3;
            Q3=makeQuery(id+"F13.imprint","IMPRINT",FACE,{"disambiguationData":[TD([[makeQuery(id+"F13.imprint","IMPRINT",EDGE,{"derivedFrom":sQuery(id+"F13.wireOp",EDGE,"E106")}),1.0]])]});
            extrude(context, id + "F14", {"entities" : qUnion([Q0, Q1, Q2, Q3]), "operationType" : NewBodyOperationType.REMOVE, "oppositeDirection" : true, "depth" : 10 * mm});
        }
        {
            var Q0;
            Q0=makeQuery(id+"F13.imprint","IMPRINT",FACE,{"disambiguationData":[TD([[makeQuery(id+"F13.imprint","IMPRINT",EDGE,{"derivedFrom":sQuery(id+"F13.wireOp",EDGE,"E100")}),1.0]])]});
            var Q1;
            Q1=makeQuery(id+"F13.imprint","IMPRINT",FACE,{"disambiguationData":[TD([[makeQuery(id+"F13.imprint","IMPRINT",EDGE,{"derivedFrom":sQuery(id+"F13.wireOp",EDGE,"E99")}),1.0]])]});
            var Q2;
            Q2=makeQuery(id+"F13.imprint","IMPRINT",FACE,{"disambiguationData":[TD([[makeQuery(id+"F13.imprint","IMPRINT",EDGE,{"derivedFrom":sQuery(id+"F13.wireOp",EDGE,"E104")}),1.0]])]});
            var Q3;
            Q3=makeQuery(id+"F13.imprint","IMPRINT",FACE,{"disambiguationData":[TD([[makeQuery(id+"F13.imprint","IMPRINT",EDGE,{"derivedFrom":sQuery(id+"F13.wireOp",EDGE,"E105")}),1.0]])]});
            extrude(context, id + "F15", {"entities" : qUnion([Q0, Q1, Q2, Q3]), "operationType" : NewBodyOperationType.ADD, "depth" : 7 * mm, "hasDraft" : true, "draftAngle" : 1 * degree, "draftPullDirection" : true});
        }
    });
